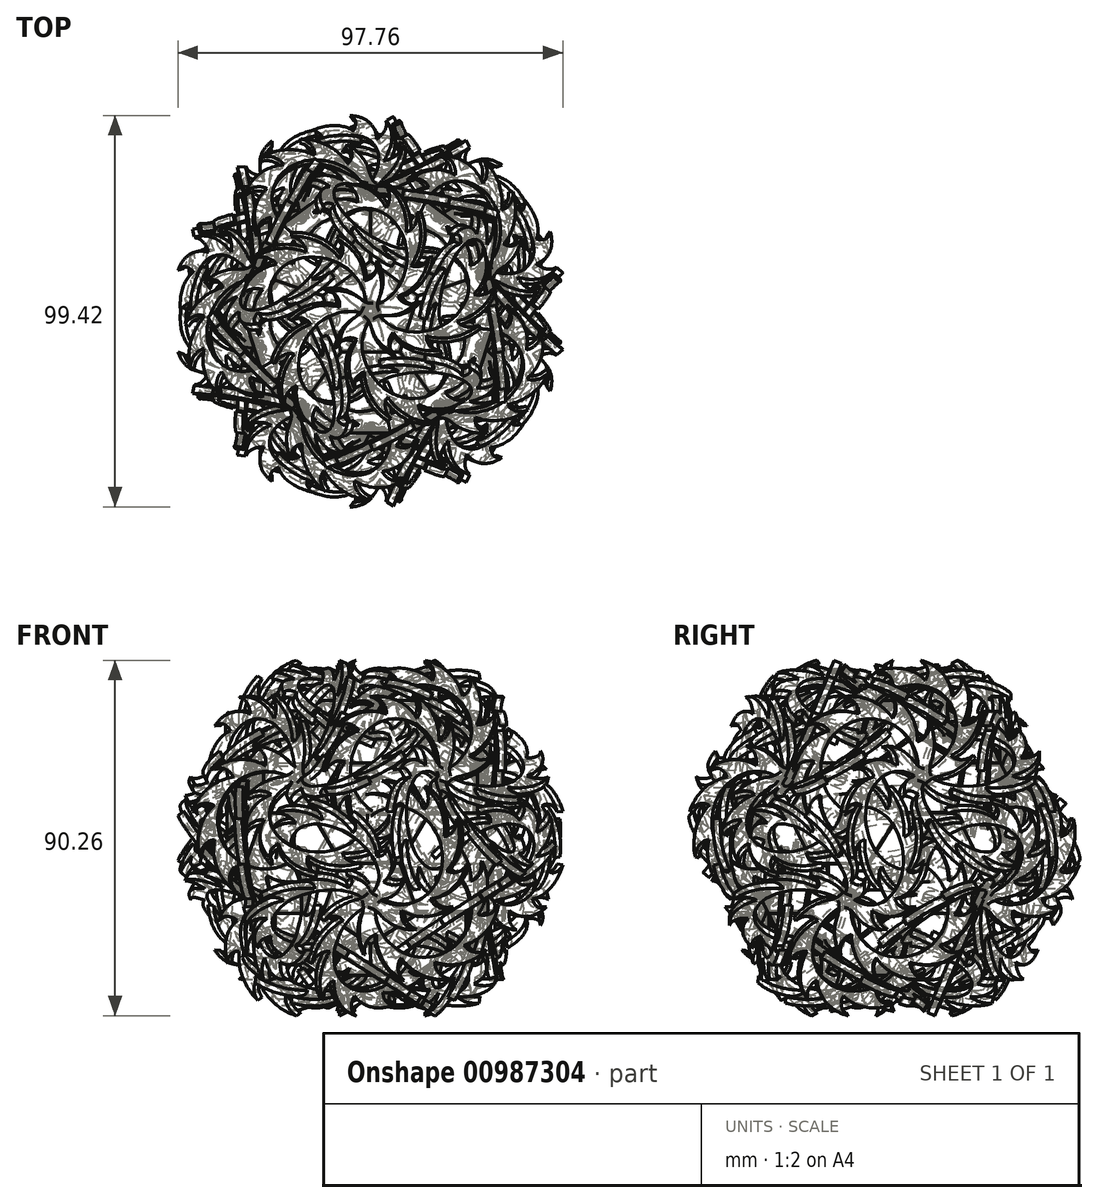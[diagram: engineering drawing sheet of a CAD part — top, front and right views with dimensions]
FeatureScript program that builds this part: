
annotation { "Feature Type Name" : "Feature", "Feature Type Description" : "" }
export const myFeature = defineFeature(function(context is Context, id is Id, definition is map)
    precondition{}
    {
        {
            var Q0;
            Q0=qCreatedBy(makeId("Top.planeOp"),FACE);
            var sketch = newSketch(context, id + "F0", { "sketchPlane" : qUnion([Q0])});
            skCircle(sketch, "E0.cCircle", {"center": v(0, 0) * mm, "radius": 10.32 * mm, "construction": true});
            skLineSegment(sketch, "E0.0", {"start": v(7.5, -10.32) * mm, "end": v(-7.5, -10.32) * mm});
            skLineSegment(sketch, "E0.1", {"start": v(-7.5, -10.32) * mm, "end": v(-12.14, 3.94) * mm});
            skLineSegment(sketch, "E0.2", {"start": v(-12.14, 3.94) * mm, "end": v(0, 12.76) * mm});
            skLineSegment(sketch, "E0.3", {"start": v(0, 12.76) * mm, "end": v(12.14, 3.94) * mm});
            skLineSegment(sketch, "E0.4", {"start": v(12.14, 3.94) * mm, "end": v(7.5, -10.32) * mm});
            skPoint(sketch, "E0.0.midPoint", {"position": v(0, -10.32) * mm});
            skLineSegment(sketch, "E1", {"start": v(0, 12.76) * mm, "end": v(0, -10.32) * mm});
            skSolve(sketch);
        }
        {
            var Q0;
            Q0=qCreatedBy(makeId("Top.planeOp"),FACE);
            var sketch = newSketch(context, id + "F1", { "sketchPlane" : qUnion([Q0])});
            skCircle(sketch, "E2.cCircle", {"center": v(22.17, -7.2) * mm, "radius": 13 * mm, "construction": true});
            skLineSegment(sketch, "E2.0", {"start": v(36.84, -4.09) * mm, "end": v(32.2, -18.35) * mm});
            skLineSegment(sketch, "E2.1", {"start": v(32.2, -18.35) * mm, "end": v(17.54, -21.47) * mm});
            skLineSegment(sketch, "E2.2", {"start": v(17.54, -21.47) * mm, "end": v(7.5, -10.32) * mm});
            skLineSegment(sketch, "E2.3", {"start": v(7.5, -10.32) * mm, "end": v(12.14, 3.94) * mm});
            skLineSegment(sketch, "E2.4", {"start": v(12.14, 3.94) * mm, "end": v(26.8, 7.06) * mm});
            skLineSegment(sketch, "E2.5", {"start": v(26.8, 7.06) * mm, "end": v(36.84, -4.09) * mm});
            skPoint(sketch, "E2.0.midPoint", {"position": v(34.53, -11.22) * mm});
            skSolve(sketch);
        }
        {
            var Q0;
            Q0=makeQuery(id+"F0.imprint","IMPRINT",FACE,{"disambiguationData":[TD([[makeQuery(id+"F0.imprint","IMPRINT",EDGE,{"derivedFrom":sQuery(id+"F0.wireOp",EDGE,"E0.0")}),-1.0]])]});
            extrude(context, id + "F2", {"entities" : qUnion([Q0]), "oppositeDirection" : true, "depth" : 1 * mm, "offsetDistance" : 25 * mm});
        }
        {
            var Q0;
            Q0=makeQuery(id+"F1.imprint","IMPRINT",FACE,{"disambiguationData":[TD([[makeQuery(id+"F1.imprint","IMPRINT",EDGE,{"derivedFrom":sQuery(id+"F1.wireOp",EDGE,"E2.0")}),-1.0]])]});
            extrude(context, id + "F3", {"entities" : qUnion([Q0]), "oppositeDirection" : true, "depth" : 1 * mm, "offsetDistance" : 25 * mm});
        }
        {
            var Q0;
            Q0=makeQuery(id+"F3.opExtrude","SWEPT_BODY",BODY,{"disambiguationData":[OSD([sQuery(id+"F1.wireOp",EDGE,"E2.0"),sQuery(id+"F1.wireOp",EDGE,"E2.1"),sQuery(id+"F1.wireOp",EDGE,"E2.2"),sQuery(id+"F1.wireOp",EDGE,"E2.3"),sQuery(id+"F1.wireOp",EDGE,"E2.4"),sQuery(id+"F1.wireOp",EDGE,"E2.5")])]});
            var Q1;
            Q1=makeQuery(id+"F2.opExtrude","CAP_EDGE",EDGE,{"disambiguationData":[OSD([sQuery(id+"F0.wireOp",EDGE,"E0.4")])],"isStart":true});
            transform(context, id + "F4", {"entities" : qUnion([Q0]), "transformType" : TransformType.ROTATION, "transformAxis" : qUnion([Q1]), "angle" : 37.38 * degree, "oppositeDirection" : true, "makeCopy" : false});
        }
        {
            var Q0;
            Q0=qCreatedBy(makeId("Right.planeOp"),FACE);
            var sketch = newSketch(context, id + "F5", { "sketchPlane" : qUnion([Q0])});
            skLineSegment(sketch, "E3", {"start": v(0, 0) * mm, "end": v(0, 7.73) * mm});
            skSolve(sketch);
        }
        {
            var Q0;
            Q0=makeQuery(id+"F3.opExtrude","SWEPT_BODY",BODY,{"disambiguationData":[OSD([sQuery(id+"F1.wireOp",EDGE,"E2.0"),sQuery(id+"F1.wireOp",EDGE,"E2.1"),sQuery(id+"F1.wireOp",EDGE,"E2.2"),sQuery(id+"F1.wireOp",EDGE,"E2.3"),sQuery(id+"F1.wireOp",EDGE,"E2.4"),sQuery(id+"F1.wireOp",EDGE,"E2.5")])]});
            var Q1;
            Q1=sQuery(id+"F5.wireOp",EDGE,"E3");
            circularPattern(context, id + "F6", {"entities" : qUnion([Q0]), "axis" : qUnion([Q1]), "angle" : 72 * degree, "instanceCount" : round(5)});
        }
        {
            var Q0;
            Q0=makeQuery(id+"F6.opPattern","COPY",FACE,{"derivedFrom":makeQuery(id+"F3.opExtrude","CAP_FACE",FACE,{"disambiguationData":[OSD([sQuery(id+"F1.wireOp",EDGE,"E2.0"),sQuery(id+"F1.wireOp",EDGE,"E2.1"),sQuery(id+"F1.wireOp",EDGE,"E2.2"),sQuery(id+"F1.wireOp",EDGE,"E2.3"),sQuery(id+"F1.wireOp",EDGE,"E2.4"),sQuery(id+"F1.wireOp",EDGE,"E2.5")])],"isStart":true}),"instanceName":"4"});
            var sketch = newSketch(context, id + "F7", { "sketchPlane" : qUnion([Q0])});
            skLineSegment(sketch, "E4", {"start": v(0, -34.18) * mm, "end": v(0, -8.2) * mm});
            skLineSegment(sketch, "E5", {"start": v(-15, -21.2) * mm, "end": v(15, -21.2) * mm});
            skCircle(sketch, "E6", {"center": v(0, -21.2) * mm, "radius": 3.24 * mm});
            skSolve(sketch);
        }
        {
            var Q0;
            Q0=qCreatedBy(makeId("Right.planeOp"),FACE);
            var sketch = newSketch(context, id + "F8", { "sketchPlane" : qUnion([Q0])});
            skArc(sketch, "E7.0", {"start": v(-1.37, 0) * mm, "mid": v(-18.04, 14.75) * mm, "end": v(-20.04, -7.42) * mm});
            skLineSegment(sketch, "E8", {"start": v(-20.04, -7.42) * mm, "end": v(-24.47, -10.8) * mm});
            skLineSegment(sketch, "E9", {"start": v(-1.37, 0) * mm, "end": v(0, 0) * mm});
            skArc(sketch, "E10", {"start": v(1.07, 1.27) * mm, "mid": v(3.46, 7.37) * mm, "end": v(2.5, 13.85) * mm});
            skArc(sketch, "E11", {"start": v(-0.8, 8.97) * mm, "mid": v(1.84, 10.74) * mm, "end": v(2.5, 13.85) * mm});
            skArc(sketch, "E12.1.0", {"start": v(-0.8, 8.97) * mm, "mid": v(-2.13, 15.94) * mm, "end": v(-6.98, 21.1) * mm});
            skArc(sketch, "E12.1.1", {"start": v(-6.75, 15.32) * mm, "mid": v(-5.72, 18.26) * mm, "end": v(-6.98, 21.1) * mm});
            skArc(sketch, "E12.2.0", {"start": v(-6.75, 15.32) * mm, "mid": v(-11.92, 20.18) * mm, "end": v(-18.89, 21.5) * mm});
            skArc(sketch, "E12.2.1", {"start": v(-15.3, 16.96) * mm, "mid": v(-16.2, 19.94) * mm, "end": v(-18.89, 21.5) * mm});
            skArc(sketch, "E12.3.0", {"start": v(-15.3, 16.96) * mm, "mid": v(-22.34, 17.85) * mm, "end": v(-28.75, 14.83) * mm});
            skArc(sketch, "E12.3.1", {"start": v(-23.18, 13.26) * mm, "mid": v(-25.66, 15.15) * mm, "end": v(-28.75, 14.83) * mm});
            skArc(sketch, "E12.4.0", {"start": v(-23.18, 13.26) * mm, "mid": v(-29.4, 9.84) * mm, "end": v(-32.81, 3.63) * mm});
            skArc(sketch, "E12.4.1", {"start": v(-27.38, 5.64) * mm, "mid": v(-30.5, 5.7) * mm, "end": v(-32.81, 3.63) * mm});
            skArc(sketch, "E12.5.0", {"start": v(-27.38, 5.64) * mm, "mid": v(-30.4, -0.78) * mm, "end": v(-29.51, -7.81) * mm});
            skArc(sketch, "E12.5.1", {"start": v(-26.3, -3) * mm, "mid": v(-28.86, -4.77) * mm, "end": v(-29.51, -7.81) * mm});
            skArc(sketch, "E12.6.0", {"start": v(-26.3, -3) * mm, "mid": v(-26.03, -7.06) * mm, "end": v(-24.49, -10.82) * mm});
            skArc(sketch, "E13", {"start": v(-24.49, -10.82) * mm, "mid": v(-20.56, -11.35) * mm, "end": v(-20.04, -7.42) * mm});
            skArc(sketch, "E14", {"start": v(-1.37, 0) * mm, "mid": v(1.27, -2.11) * mm, "end": v(1.07, 1.27) * mm});
            skSolve(sketch);
        }
        {
            var Q0;
            {var subQ2=sQuery(id+"F8.wireOp",EDGE,"E7.0");Q0=makeQuery(id+"F8.imprint","IMPRINT",FACE,{"disambiguationData":[TD([[makeQuery(id+"F8.imprint","IMPRINT",EDGE,{"derivedFrom":subQ2}),-1.0]])]});}
            extrude(context, id + "F9", {"entities" : qUnion([Q0]), "oppositeDirection" : true, "depth" : 2 * mm});
        }
        {
            var Q0;
            Q0=makeQuery(id+"F9.opExtrude","SWEPT_EDGE",EDGE,{"disambiguationData":[OSD([sQuery(id+"F8.wireOp",EDGE,"E10"),sQuery(id+"F8.wireOp",EDGE,"E14")])]});
            fillet(context, id + "F10", {"entities" : qUnion([Q0]), "radius" : 5 * mm, "tangentPropagation" : true, "allowEdgeOverflow" : false});
        }
        {
            var Q0;
            Q0=qCreatedBy(makeId("Right.planeOp"),FACE);
            var sketch = newSketch(context, id + "F11", { "sketchPlane" : qUnion([Q0])});
            skLineSegment(sketch, "E15", {"start": v(0, 0) * mm, "end": v(-20.65, -7.89) * mm});
            skLineSegment(sketch, "E16", {"start": v(0, 0) * mm, "end": v(0, 28.42) * mm});
            skSolve(sketch);
        }
        {
            var Q0;
            Q0=makeQuery(id+"F9.opExtrude","SWEPT_BODY",BODY,{"disambiguationData":[OSD([sQuery(id+"F8.wireOp",EDGE,"003f2e54-bd62-4f0b-a98e-8c36e71e2cf6"),sQuery(id+"F8.wireOp",EDGE,"8c729305-40a1-49fa-b790-4b99a3909bb6"),sQuery(id+"F8.wireOp",EDGE,"862a2a8f-3db7-4421-9c69-6ab2f53c4c24.1.0"),sQuery(id+"F8.wireOp",EDGE,"862a2a8f-3db7-4421-9c69-6ab2f53c4c24.1.1"),sQuery(id+"F8.wireOp",EDGE,"862a2a8f-3db7-4421-9c69-6ab2f53c4c24.2.0"),sQuery(id+"F8.wireOp",EDGE,"862a2a8f-3db7-4421-9c69-6ab2f53c4c24.2.1"),sQuery(id+"F8.wireOp",EDGE,"862a2a8f-3db7-4421-9c69-6ab2f53c4c24.3.0"),sQuery(id+"F8.wireOp",EDGE,"862a2a8f-3db7-4421-9c69-6ab2f53c4c24.3.1"),sQuery(id+"F8.wireOp",EDGE,"862a2a8f-3db7-4421-9c69-6ab2f53c4c24.4.0"),sQuery(id+"F8.wireOp",EDGE,"862a2a8f-3db7-4421-9c69-6ab2f53c4c24.4.1"),sQuery(id+"F8.wireOp",EDGE,"862a2a8f-3db7-4421-9c69-6ab2f53c4c24.5.0"),sQuery(id+"F8.wireOp",EDGE,"E7.0"),sQuery(id+"F8.wireOp",EDGE,"E8"),sQuery(id+"F8.wireOp",EDGE,"E9")])]});
            var Q1;
            Q1=sQuery(id+"F11.wireOp",EDGE,"E15");
            transform(context, id + "F12", {"entities" : qUnion([Q0]), "transformType" : TransformType.ROTATION, "transformAxis" : qUnion([Q1]), "angle" : 65 * degree, "makeCopy" : false});
        }
        {
            var Q0;
            Q0=makeQuery(id+"F9.opExtrude","SWEPT_BODY",BODY,{"disambiguationData":[OSD([sQuery(id+"F8.wireOp",EDGE,"003f2e54-bd62-4f0b-a98e-8c36e71e2cf6"),sQuery(id+"F8.wireOp",EDGE,"8c729305-40a1-49fa-b790-4b99a3909bb6"),sQuery(id+"F8.wireOp",EDGE,"862a2a8f-3db7-4421-9c69-6ab2f53c4c24.1.0"),sQuery(id+"F8.wireOp",EDGE,"862a2a8f-3db7-4421-9c69-6ab2f53c4c24.1.1"),sQuery(id+"F8.wireOp",EDGE,"862a2a8f-3db7-4421-9c69-6ab2f53c4c24.2.0"),sQuery(id+"F8.wireOp",EDGE,"862a2a8f-3db7-4421-9c69-6ab2f53c4c24.2.1"),sQuery(id+"F8.wireOp",EDGE,"862a2a8f-3db7-4421-9c69-6ab2f53c4c24.3.0"),sQuery(id+"F8.wireOp",EDGE,"862a2a8f-3db7-4421-9c69-6ab2f53c4c24.3.1"),sQuery(id+"F8.wireOp",EDGE,"862a2a8f-3db7-4421-9c69-6ab2f53c4c24.4.0"),sQuery(id+"F8.wireOp",EDGE,"862a2a8f-3db7-4421-9c69-6ab2f53c4c24.4.1"),sQuery(id+"F8.wireOp",EDGE,"862a2a8f-3db7-4421-9c69-6ab2f53c4c24.5.0"),sQuery(id+"F8.wireOp",EDGE,"E7.0"),sQuery(id+"F8.wireOp",EDGE,"E8"),sQuery(id+"F8.wireOp",EDGE,"E9")])]});
            var Q1;
            Q1=sQuery(id+"F11.wireOp",EDGE,"E16");
            circularPattern(context, id + "F13", {"entities" : qUnion([Q0]), "axis" : qUnion([Q1]), "angle" : 72 * degree, "instanceCount" : round(5)});
        }
        {
            var Q0;
            Q0=qCreatedBy(makeId("Right.planeOp"),FACE);
            var sketch = newSketch(context, id + "F14", { "sketchPlane" : qUnion([Q0])});
            skLineSegment(sketch, "E17.0", {"start": v(-30.97, -15.77) * mm, "end": v(-10.32, 0) * mm});
            skLineSegment(sketch, "E18", {"start": v(-20.65, -7.89) * mm, "end": v(-30.05, 4.42) * mm});
            skSolve(sketch);
        }
        {
            var Q0;
            Q0=makeQuery(id+"F9.opExtrude","SWEPT_BODY",BODY,{"disambiguationData":[OSD([sQuery(id+"F8.wireOp",EDGE,"003f2e54-bd62-4f0b-a98e-8c36e71e2cf6"),sQuery(id+"F8.wireOp",EDGE,"8c729305-40a1-49fa-b790-4b99a3909bb6"),sQuery(id+"F8.wireOp",EDGE,"862a2a8f-3db7-4421-9c69-6ab2f53c4c24.1.0"),sQuery(id+"F8.wireOp",EDGE,"862a2a8f-3db7-4421-9c69-6ab2f53c4c24.1.1"),sQuery(id+"F8.wireOp",EDGE,"862a2a8f-3db7-4421-9c69-6ab2f53c4c24.2.0"),sQuery(id+"F8.wireOp",EDGE,"862a2a8f-3db7-4421-9c69-6ab2f53c4c24.2.1"),sQuery(id+"F8.wireOp",EDGE,"862a2a8f-3db7-4421-9c69-6ab2f53c4c24.3.0"),sQuery(id+"F8.wireOp",EDGE,"862a2a8f-3db7-4421-9c69-6ab2f53c4c24.3.1"),sQuery(id+"F8.wireOp",EDGE,"862a2a8f-3db7-4421-9c69-6ab2f53c4c24.4.0"),sQuery(id+"F8.wireOp",EDGE,"862a2a8f-3db7-4421-9c69-6ab2f53c4c24.4.1"),sQuery(id+"F8.wireOp",EDGE,"862a2a8f-3db7-4421-9c69-6ab2f53c4c24.5.0"),sQuery(id+"F8.wireOp",EDGE,"E7.0"),sQuery(id+"F8.wireOp",EDGE,"E8"),sQuery(id+"F8.wireOp",EDGE,"E9")])]});
            var Q1;
            Q1=sQuery(id+"F14.wireOp",EDGE,"E18");
            circularPattern(context, id + "F15", {"entities" : qUnion([Q0]), "axis" : qUnion([Q1]), "angle" : 120 * degree, "instanceCount" : round(3)});
        }
        {
            var Q0;
            Q0=makeQuery(id+"F15.opPattern","COPY",BODY,{"derivedFrom":makeQuery(id+"F9.opExtrude","SWEPT_BODY",BODY,{"disambiguationData":[OSD([sQuery(id+"F8.wireOp",EDGE,"E7.0"),sQuery(id+"F8.wireOp",EDGE,"E10"),sQuery(id+"F8.wireOp",EDGE,"E11"),sQuery(id+"F8.wireOp",EDGE,"E12.1.0"),sQuery(id+"F8.wireOp",EDGE,"E12.1.1"),sQuery(id+"F8.wireOp",EDGE,"E12.2.0"),sQuery(id+"F8.wireOp",EDGE,"E12.2.1"),sQuery(id+"F8.wireOp",EDGE,"E12.3.0"),sQuery(id+"F8.wireOp",EDGE,"E12.3.1"),sQuery(id+"F8.wireOp",EDGE,"E12.4.0"),sQuery(id+"F8.wireOp",EDGE,"E12.4.1"),sQuery(id+"F8.wireOp",EDGE,"E12.5.0"),sQuery(id+"F8.wireOp",EDGE,"E12.5.1"),sQuery(id+"F8.wireOp",EDGE,"E12.6.0"),sQuery(id+"F8.wireOp",EDGE,"E13"),sQuery(id+"F8.wireOp",EDGE,"E14")])]}),"instanceName":"2"});
            var Q1;
            Q1=makeQuery(id+"F15.opPattern","COPY",BODY,{"derivedFrom":makeQuery(id+"F9.opExtrude","SWEPT_BODY",BODY,{"disambiguationData":[OSD([sQuery(id+"F8.wireOp",EDGE,"E7.0"),sQuery(id+"F8.wireOp",EDGE,"E10"),sQuery(id+"F8.wireOp",EDGE,"E11"),sQuery(id+"F8.wireOp",EDGE,"E12.1.0"),sQuery(id+"F8.wireOp",EDGE,"E12.1.1"),sQuery(id+"F8.wireOp",EDGE,"E12.2.0"),sQuery(id+"F8.wireOp",EDGE,"E12.2.1"),sQuery(id+"F8.wireOp",EDGE,"E12.3.0"),sQuery(id+"F8.wireOp",EDGE,"E12.3.1"),sQuery(id+"F8.wireOp",EDGE,"E12.4.0"),sQuery(id+"F8.wireOp",EDGE,"E12.4.1"),sQuery(id+"F8.wireOp",EDGE,"E12.5.0"),sQuery(id+"F8.wireOp",EDGE,"E12.5.1"),sQuery(id+"F8.wireOp",EDGE,"E12.6.0"),sQuery(id+"F8.wireOp",EDGE,"E13"),sQuery(id+"F8.wireOp",EDGE,"E14")])]}),"instanceName":"1"});
            var Q2;
            Q2=sQuery(id+"F11.wireOp",EDGE,"E16");
            circularPattern(context, id + "F16", {"entities" : qUnion([Q0, Q1]), "axis" : qUnion([Q2]), "angle" : 72 * degree, "instanceCount" : round(5)});
        }
        {
            var Q0;
            Q0=makeQuery(id+"F3.opExtrude","SWEPT_BODY",BODY,{"disambiguationData":[OSD([sQuery(id+"F1.wireOp",EDGE,"E2.0"),sQuery(id+"F1.wireOp",EDGE,"E2.1"),sQuery(id+"F1.wireOp",EDGE,"E2.2"),sQuery(id+"F1.wireOp",EDGE,"E2.3"),sQuery(id+"F1.wireOp",EDGE,"E2.4"),sQuery(id+"F1.wireOp",EDGE,"E2.5")])]});
            var Q1;
            Q1=makeQuery(id+"F16.opPattern","COPY",BODY,{"derivedFrom":makeQuery(id+"F15.opPattern","COPY",BODY,{"derivedFrom":makeQuery(id+"F9.opExtrude","SWEPT_BODY",BODY,{"disambiguationData":[OSD([sQuery(id+"F8.wireOp",EDGE,"E7.0"),sQuery(id+"F8.wireOp",EDGE,"E10"),sQuery(id+"F8.wireOp",EDGE,"E11"),sQuery(id+"F8.wireOp",EDGE,"E12.1.0"),sQuery(id+"F8.wireOp",EDGE,"E12.1.1"),sQuery(id+"F8.wireOp",EDGE,"E12.2.0"),sQuery(id+"F8.wireOp",EDGE,"E12.2.1"),sQuery(id+"F8.wireOp",EDGE,"E12.3.0"),sQuery(id+"F8.wireOp",EDGE,"E12.3.1"),sQuery(id+"F8.wireOp",EDGE,"E12.4.0"),sQuery(id+"F8.wireOp",EDGE,"E12.4.1"),sQuery(id+"F8.wireOp",EDGE,"E12.5.0"),sQuery(id+"F8.wireOp",EDGE,"E12.5.1"),sQuery(id+"F8.wireOp",EDGE,"E12.6.0"),sQuery(id+"F8.wireOp",EDGE,"E13"),sQuery(id+"F8.wireOp",EDGE,"E14")])]}),"instanceName":"1"}),"instanceName":"1"});
            var Q2;
            Q2=makeQuery(id+"F13.opPattern","COPY",BODY,{"derivedFrom":makeQuery(id+"F9.opExtrude","SWEPT_BODY",BODY,{"disambiguationData":[OSD([sQuery(id+"F8.wireOp",EDGE,"E7.0"),sQuery(id+"F8.wireOp",EDGE,"E10"),sQuery(id+"F8.wireOp",EDGE,"E11"),sQuery(id+"F8.wireOp",EDGE,"E12.1.0"),sQuery(id+"F8.wireOp",EDGE,"E12.1.1"),sQuery(id+"F8.wireOp",EDGE,"E12.2.0"),sQuery(id+"F8.wireOp",EDGE,"E12.2.1"),sQuery(id+"F8.wireOp",EDGE,"E12.3.0"),sQuery(id+"F8.wireOp",EDGE,"E12.3.1"),sQuery(id+"F8.wireOp",EDGE,"E12.4.0"),sQuery(id+"F8.wireOp",EDGE,"E12.4.1"),sQuery(id+"F8.wireOp",EDGE,"E12.5.0"),sQuery(id+"F8.wireOp",EDGE,"E12.5.1"),sQuery(id+"F8.wireOp",EDGE,"E12.6.0"),sQuery(id+"F8.wireOp",EDGE,"E13"),sQuery(id+"F8.wireOp",EDGE,"E14")])]}),"instanceName":"1"});
            var Q3;
            Q3=makeQuery(id+"F16.opPattern","COPY",BODY,{"derivedFrom":makeQuery(id+"F15.opPattern","COPY",BODY,{"derivedFrom":makeQuery(id+"F9.opExtrude","SWEPT_BODY",BODY,{"disambiguationData":[OSD([sQuery(id+"F8.wireOp",EDGE,"E7.0"),sQuery(id+"F8.wireOp",EDGE,"E10"),sQuery(id+"F8.wireOp",EDGE,"E11"),sQuery(id+"F8.wireOp",EDGE,"E12.1.0"),sQuery(id+"F8.wireOp",EDGE,"E12.1.1"),sQuery(id+"F8.wireOp",EDGE,"E12.2.0"),sQuery(id+"F8.wireOp",EDGE,"E12.2.1"),sQuery(id+"F8.wireOp",EDGE,"E12.3.0"),sQuery(id+"F8.wireOp",EDGE,"E12.3.1"),sQuery(id+"F8.wireOp",EDGE,"E12.4.0"),sQuery(id+"F8.wireOp",EDGE,"E12.4.1"),sQuery(id+"F8.wireOp",EDGE,"E12.5.0"),sQuery(id+"F8.wireOp",EDGE,"E12.5.1"),sQuery(id+"F8.wireOp",EDGE,"E12.6.0"),sQuery(id+"F8.wireOp",EDGE,"E13"),sQuery(id+"F8.wireOp",EDGE,"E14")])]}),"instanceName":"2"}),"instanceName":"1"});
            var Q4;
            Q4=sQuery(id+"F14.wireOp",EDGE,"E18");
            circularPattern(context, id + "F17", {"entities" : qUnion([Q0, Q1, Q2, Q3]), "axis" : qUnion([Q4]), "angle" : 120 * degree, "instanceCount" : 2, "oppositeDirection" : true});
        }
        {
            var Q0;
            Q0=makeQuery(id+"F2.opExtrude","SWEPT_BODY",BODY,{"disambiguationData":[OSD([sQuery(id+"F0.wireOp",EDGE,"E0.0"),sQuery(id+"F0.wireOp",EDGE,"E0.1"),sQuery(id+"F0.wireOp",EDGE,"E0.2"),sQuery(id+"F0.wireOp",EDGE,"E0.3"),sQuery(id+"F0.wireOp",EDGE,"E0.4")])]});
            var Q1;
            Q1=makeQuery(id+"F13.opPattern","COPY",BODY,{"derivedFrom":makeQuery(id+"F9.opExtrude","SWEPT_BODY",BODY,{"disambiguationData":[OSD([sQuery(id+"F8.wireOp",EDGE,"E7.0"),sQuery(id+"F8.wireOp",EDGE,"E10"),sQuery(id+"F8.wireOp",EDGE,"E11"),sQuery(id+"F8.wireOp",EDGE,"E12.1.0"),sQuery(id+"F8.wireOp",EDGE,"E12.1.1"),sQuery(id+"F8.wireOp",EDGE,"E12.2.0"),sQuery(id+"F8.wireOp",EDGE,"E12.2.1"),sQuery(id+"F8.wireOp",EDGE,"E12.3.0"),sQuery(id+"F8.wireOp",EDGE,"E12.3.1"),sQuery(id+"F8.wireOp",EDGE,"E12.4.0"),sQuery(id+"F8.wireOp",EDGE,"E12.4.1"),sQuery(id+"F8.wireOp",EDGE,"E12.5.0"),sQuery(id+"F8.wireOp",EDGE,"E12.5.1"),sQuery(id+"F8.wireOp",EDGE,"E12.6.0"),sQuery(id+"F8.wireOp",EDGE,"E13"),sQuery(id+"F8.wireOp",EDGE,"E14")])]}),"instanceName":"2"});
            var Q2;
            Q2=makeQuery(id+"F13.opPattern","COPY",BODY,{"derivedFrom":makeQuery(id+"F9.opExtrude","SWEPT_BODY",BODY,{"disambiguationData":[OSD([sQuery(id+"F8.wireOp",EDGE,"E7.0"),sQuery(id+"F8.wireOp",EDGE,"E10"),sQuery(id+"F8.wireOp",EDGE,"E11"),sQuery(id+"F8.wireOp",EDGE,"E12.1.0"),sQuery(id+"F8.wireOp",EDGE,"E12.1.1"),sQuery(id+"F8.wireOp",EDGE,"E12.2.0"),sQuery(id+"F8.wireOp",EDGE,"E12.2.1"),sQuery(id+"F8.wireOp",EDGE,"E12.3.0"),sQuery(id+"F8.wireOp",EDGE,"E12.3.1"),sQuery(id+"F8.wireOp",EDGE,"E12.4.0"),sQuery(id+"F8.wireOp",EDGE,"E12.4.1"),sQuery(id+"F8.wireOp",EDGE,"E12.5.0"),sQuery(id+"F8.wireOp",EDGE,"E12.5.1"),sQuery(id+"F8.wireOp",EDGE,"E12.6.0"),sQuery(id+"F8.wireOp",EDGE,"E13"),sQuery(id+"F8.wireOp",EDGE,"E14")])]}),"instanceName":"3"});
            var Q3;
            Q3=sQuery(id+"F14.wireOp",EDGE,"E18");
            circularPattern(context, id + "F18", {"entities" : qUnion([Q0, Q1, Q2]), "axis" : qUnion([Q3]), "angle" : 120 * degree, "instanceCount" : round(3)});
        }
        {
            var Q0;
            Q0=makeQuery(id+"F18.opPattern","COPY",FACE,{"derivedFrom":makeQuery(id+"F2.opExtrude","CAP_FACE",FACE,{"disambiguationData":[OSD([sQuery(id+"F0.wireOp",EDGE,"E0.0"),sQuery(id+"F0.wireOp",EDGE,"E0.1"),sQuery(id+"F0.wireOp",EDGE,"E0.2"),sQuery(id+"F0.wireOp",EDGE,"E0.3"),sQuery(id+"F0.wireOp",EDGE,"E0.4")])],"isStart":true}),"instanceName":"1"});
            var sketch = newSketch(context, id + "F19", { "sketchPlane" : qUnion([Q0])});
            skLineSegment(sketch, "E19", {"start": v(-1.3, -23.63) * mm, "end": v(-19.97, -37.2) * mm});
            skLineSegment(sketch, "E20", {"start": v(-19.97, -22.2) * mm, "end": v(-1.3, -35.77) * mm});
            skSolve(sketch);
        }
        {
            var Q0;
            Q0=sQuery(id+"F19.wireOp",VERTEX,"E19.end");
            var Q1;
            Q1=sQuery(id+"F19.wireOp",VERTEX,"E19.start");
            var Q2;
            Q2=sQuery(id+"F14.wireOp",VERTEX,"E18.end");
            cPlane(context, id + "F20", {"entities" : qUnion([Q0, Q1, Q2]), "cplaneType" : CPlaneType.THREE_POINT, "offset" : 150 * mm, "width" : 150 * mm, "height" : 150 * mm});
        }
        {
            var Q0;
            Q0=qCreatedBy(id+"F20.planeOp",FACE);
            var sketch = newSketch(context, id + "F21", { "sketchPlane" : qUnion([Q0])});
            skLineSegment(sketch, "E21.0", {"start": v(23.59, 6.27) * mm, "end": v(41.93, -7.75) * mm});
            skLineSegment(sketch, "E21.1", {"start": v(34.92, -2.4) * mm, "end": v(29.26, 1.94) * mm});
            skLineSegment(sketch, "E22", {"start": v(31.8, 0) * mm, "end": v(33.22, 1.87) * mm});
            skLineSegment(sketch, "E23", {"start": v(33.22, 1.87) * mm, "end": v(37.58, 7.58) * mm});
            skSolve(sketch);
        }
        {
            var Q0;
            Q0=makeQuery(id+"F17.opPattern","COPY",BODY,{"derivedFrom":makeQuery(id+"F3.opExtrude","SWEPT_BODY",BODY,{"disambiguationData":[OSD([sQuery(id+"F1.wireOp",EDGE,"E2.0"),sQuery(id+"F1.wireOp",EDGE,"E2.1"),sQuery(id+"F1.wireOp",EDGE,"E2.2"),sQuery(id+"F1.wireOp",EDGE,"E2.3"),sQuery(id+"F1.wireOp",EDGE,"E2.4"),sQuery(id+"F1.wireOp",EDGE,"E2.5")])]}),"instanceName":"1"});
            var Q1;
            Q1=makeQuery(id+"F17.opPattern","COPY",BODY,{"derivedFrom":makeQuery(id+"F13.opPattern","COPY",BODY,{"derivedFrom":makeQuery(id+"F9.opExtrude","SWEPT_BODY",BODY,{"disambiguationData":[OSD([sQuery(id+"F8.wireOp",EDGE,"E7.0"),sQuery(id+"F8.wireOp",EDGE,"E10"),sQuery(id+"F8.wireOp",EDGE,"E11"),sQuery(id+"F8.wireOp",EDGE,"E12.1.0"),sQuery(id+"F8.wireOp",EDGE,"E12.1.1"),sQuery(id+"F8.wireOp",EDGE,"E12.2.0"),sQuery(id+"F8.wireOp",EDGE,"E12.2.1"),sQuery(id+"F8.wireOp",EDGE,"E12.3.0"),sQuery(id+"F8.wireOp",EDGE,"E12.3.1"),sQuery(id+"F8.wireOp",EDGE,"E12.4.0"),sQuery(id+"F8.wireOp",EDGE,"E12.4.1"),sQuery(id+"F8.wireOp",EDGE,"E12.5.0"),sQuery(id+"F8.wireOp",EDGE,"E12.5.1"),sQuery(id+"F8.wireOp",EDGE,"E12.6.0"),sQuery(id+"F8.wireOp",EDGE,"E13"),sQuery(id+"F8.wireOp",EDGE,"E14")])]}),"instanceName":"1"}),"instanceName":"1"});
            var Q2;
            Q2=makeQuery(id+"F17.opPattern","COPY",BODY,{"derivedFrom":makeQuery(id+"F16.opPattern","COPY",BODY,{"derivedFrom":makeQuery(id+"F15.opPattern","COPY",BODY,{"derivedFrom":makeQuery(id+"F9.opExtrude","SWEPT_BODY",BODY,{"disambiguationData":[OSD([sQuery(id+"F8.wireOp",EDGE,"E7.0"),sQuery(id+"F8.wireOp",EDGE,"E10"),sQuery(id+"F8.wireOp",EDGE,"E11"),sQuery(id+"F8.wireOp",EDGE,"E12.1.0"),sQuery(id+"F8.wireOp",EDGE,"E12.1.1"),sQuery(id+"F8.wireOp",EDGE,"E12.2.0"),sQuery(id+"F8.wireOp",EDGE,"E12.2.1"),sQuery(id+"F8.wireOp",EDGE,"E12.3.0"),sQuery(id+"F8.wireOp",EDGE,"E12.3.1"),sQuery(id+"F8.wireOp",EDGE,"E12.4.0"),sQuery(id+"F8.wireOp",EDGE,"E12.4.1"),sQuery(id+"F8.wireOp",EDGE,"E12.5.0"),sQuery(id+"F8.wireOp",EDGE,"E12.5.1"),sQuery(id+"F8.wireOp",EDGE,"E12.6.0"),sQuery(id+"F8.wireOp",EDGE,"E13"),sQuery(id+"F8.wireOp",EDGE,"E14")])]}),"instanceName":"2"}),"instanceName":"1"}),"instanceName":"1"});
            var Q3;
            Q3=makeQuery(id+"F17.opPattern","COPY",BODY,{"derivedFrom":makeQuery(id+"F16.opPattern","COPY",BODY,{"derivedFrom":makeQuery(id+"F15.opPattern","COPY",BODY,{"derivedFrom":makeQuery(id+"F9.opExtrude","SWEPT_BODY",BODY,{"disambiguationData":[OSD([sQuery(id+"F8.wireOp",EDGE,"E7.0"),sQuery(id+"F8.wireOp",EDGE,"E10"),sQuery(id+"F8.wireOp",EDGE,"E11"),sQuery(id+"F8.wireOp",EDGE,"E12.1.0"),sQuery(id+"F8.wireOp",EDGE,"E12.1.1"),sQuery(id+"F8.wireOp",EDGE,"E12.2.0"),sQuery(id+"F8.wireOp",EDGE,"E12.2.1"),sQuery(id+"F8.wireOp",EDGE,"E12.3.0"),sQuery(id+"F8.wireOp",EDGE,"E12.3.1"),sQuery(id+"F8.wireOp",EDGE,"E12.4.0"),sQuery(id+"F8.wireOp",EDGE,"E12.4.1"),sQuery(id+"F8.wireOp",EDGE,"E12.5.0"),sQuery(id+"F8.wireOp",EDGE,"E12.5.1"),sQuery(id+"F8.wireOp",EDGE,"E12.6.0"),sQuery(id+"F8.wireOp",EDGE,"E13"),sQuery(id+"F8.wireOp",EDGE,"E14")])]}),"instanceName":"1"}),"instanceName":"1"}),"instanceName":"1"});
            var Q4;
            Q4=sQuery(id+"F21.wireOp",EDGE,"E22");
            circularPattern(context, id + "F22", {"entities" : qUnion([Q0, Q1, Q2, Q3]), "axis" : qUnion([Q4]), "angle" : 72 * degree, "instanceCount" : round(3), "oppositeDirection" : true});
        }
        {
            var Q0;
            Q0=makeQuery(id+"F18.opPattern","COPY",FACE,{"derivedFrom":makeQuery(id+"F2.opExtrude","CAP_FACE",FACE,{"disambiguationData":[OSD([sQuery(id+"F0.wireOp",EDGE,"E0.0"),sQuery(id+"F0.wireOp",EDGE,"E0.1"),sQuery(id+"F0.wireOp",EDGE,"E0.2"),sQuery(id+"F0.wireOp",EDGE,"E0.3"),sQuery(id+"F0.wireOp",EDGE,"E0.4")])],"isStart":true}),"instanceName":"2"});
            var sketch = newSketch(context, id + "F23", { "sketchPlane" : qUnion([Q0])});
            skLineSegment(sketch, "E24", {"start": v(1.3, -23.63) * mm, "end": v(19.97, -37.2) * mm});
            skLineSegment(sketch, "E25", {"start": v(5.7, -41.83) * mm, "end": v(12.84, -19.88) * mm});
            skSolve(sketch);
        }
        {
            var Q0;
            Q0=sQuery(id+"F23.wireOp",VERTEX,"E24.end");
            var Q1;
            Q1=sQuery(id+"F23.wireOp",VERTEX,"E24.start");
            var Q2;
            Q2=sQuery(id+"F14.wireOp",VERTEX,"E18.end");
            cPlane(context, id + "F24", {"entities" : qUnion([Q0, Q1, Q2]), "cplaneType" : CPlaneType.THREE_POINT, "offset" : 150 * mm, "width" : 150 * mm, "height" : 150 * mm});
        }
        {
            var Q0;
            Q0=qCreatedBy(id+"F24.planeOp",FACE);
            var sketch = newSketch(context, id + "F25", { "sketchPlane" : qUnion([Q0])});
            skLineSegment(sketch, "E26.0", {"start": v(23.59, 6.27) * mm, "end": v(41.93, -7.75) * mm});
            skLineSegment(sketch, "E26.1", {"start": v(34.92, -2.4) * mm, "end": v(29.26, 1.94) * mm});
            skLineSegment(sketch, "E27", {"start": v(31.8, 0) * mm, "end": v(36.23, 5.8) * mm});
            skSolve(sketch);
        }
        {
            var Q0;
            Q0=makeQuery(id+"F3.opExtrude","SWEPT_BODY",BODY,{"disambiguationData":[OSD([sQuery(id+"F1.wireOp",EDGE,"E2.0"),sQuery(id+"F1.wireOp",EDGE,"E2.1"),sQuery(id+"F1.wireOp",EDGE,"E2.2"),sQuery(id+"F1.wireOp",EDGE,"E2.3"),sQuery(id+"F1.wireOp",EDGE,"E2.4"),sQuery(id+"F1.wireOp",EDGE,"E2.5")])]});
            var Q1;
            Q1=makeQuery(id+"F16.opPattern","COPY",BODY,{"derivedFrom":makeQuery(id+"F15.opPattern","COPY",BODY,{"derivedFrom":makeQuery(id+"F9.opExtrude","SWEPT_BODY",BODY,{"disambiguationData":[OSD([sQuery(id+"F8.wireOp",EDGE,"E7.0"),sQuery(id+"F8.wireOp",EDGE,"E10"),sQuery(id+"F8.wireOp",EDGE,"E11"),sQuery(id+"F8.wireOp",EDGE,"E12.1.0"),sQuery(id+"F8.wireOp",EDGE,"E12.1.1"),sQuery(id+"F8.wireOp",EDGE,"E12.2.0"),sQuery(id+"F8.wireOp",EDGE,"E12.2.1"),sQuery(id+"F8.wireOp",EDGE,"E12.3.0"),sQuery(id+"F8.wireOp",EDGE,"E12.3.1"),sQuery(id+"F8.wireOp",EDGE,"E12.4.0"),sQuery(id+"F8.wireOp",EDGE,"E12.4.1"),sQuery(id+"F8.wireOp",EDGE,"E12.5.0"),sQuery(id+"F8.wireOp",EDGE,"E12.5.1"),sQuery(id+"F8.wireOp",EDGE,"E12.6.0"),sQuery(id+"F8.wireOp",EDGE,"E13"),sQuery(id+"F8.wireOp",EDGE,"E14")])]}),"instanceName":"2"}),"instanceName":"1"});
            var Q2;
            Q2=makeQuery(id+"F13.opPattern","COPY",BODY,{"derivedFrom":makeQuery(id+"F9.opExtrude","SWEPT_BODY",BODY,{"disambiguationData":[OSD([sQuery(id+"F8.wireOp",EDGE,"E7.0"),sQuery(id+"F8.wireOp",EDGE,"E10"),sQuery(id+"F8.wireOp",EDGE,"E11"),sQuery(id+"F8.wireOp",EDGE,"E12.1.0"),sQuery(id+"F8.wireOp",EDGE,"E12.1.1"),sQuery(id+"F8.wireOp",EDGE,"E12.2.0"),sQuery(id+"F8.wireOp",EDGE,"E12.2.1"),sQuery(id+"F8.wireOp",EDGE,"E12.3.0"),sQuery(id+"F8.wireOp",EDGE,"E12.3.1"),sQuery(id+"F8.wireOp",EDGE,"E12.4.0"),sQuery(id+"F8.wireOp",EDGE,"E12.4.1"),sQuery(id+"F8.wireOp",EDGE,"E12.5.0"),sQuery(id+"F8.wireOp",EDGE,"E12.5.1"),sQuery(id+"F8.wireOp",EDGE,"E12.6.0"),sQuery(id+"F8.wireOp",EDGE,"E13"),sQuery(id+"F8.wireOp",EDGE,"E14")])]}),"instanceName":"1"});
            var Q3;
            Q3=makeQuery(id+"F16.opPattern","COPY",BODY,{"derivedFrom":makeQuery(id+"F15.opPattern","COPY",BODY,{"derivedFrom":makeQuery(id+"F9.opExtrude","SWEPT_BODY",BODY,{"disambiguationData":[OSD([sQuery(id+"F8.wireOp",EDGE,"E7.0"),sQuery(id+"F8.wireOp",EDGE,"E10"),sQuery(id+"F8.wireOp",EDGE,"E11"),sQuery(id+"F8.wireOp",EDGE,"E12.1.0"),sQuery(id+"F8.wireOp",EDGE,"E12.1.1"),sQuery(id+"F8.wireOp",EDGE,"E12.2.0"),sQuery(id+"F8.wireOp",EDGE,"E12.2.1"),sQuery(id+"F8.wireOp",EDGE,"E12.3.0"),sQuery(id+"F8.wireOp",EDGE,"E12.3.1"),sQuery(id+"F8.wireOp",EDGE,"E12.4.0"),sQuery(id+"F8.wireOp",EDGE,"E12.4.1"),sQuery(id+"F8.wireOp",EDGE,"E12.5.0"),sQuery(id+"F8.wireOp",EDGE,"E12.5.1"),sQuery(id+"F8.wireOp",EDGE,"E12.6.0"),sQuery(id+"F8.wireOp",EDGE,"E13"),sQuery(id+"F8.wireOp",EDGE,"E14")])]}),"instanceName":"1"}),"instanceName":"1"});
            var Q4;
            Q4=sQuery(id+"F25.wireOp",EDGE,"E27");
            circularPattern(context, id + "F26", {"entities" : qUnion([Q0, Q1, Q2, Q3]), "axis" : qUnion([Q4]), "angle" : 72 * degree, "instanceCount" : round(3), "oppositeDirection" : true});
        }
        {
            var Q0;
            Q0=makeQuery(id+"F17.opPattern","COPY",FACE,{"derivedFrom":makeQuery(id+"F3.opExtrude","CAP_FACE",FACE,{"disambiguationData":[OSD([sQuery(id+"F1.wireOp",EDGE,"E2.0"),sQuery(id+"F1.wireOp",EDGE,"E2.1"),sQuery(id+"F1.wireOp",EDGE,"E2.2"),sQuery(id+"F1.wireOp",EDGE,"E2.3"),sQuery(id+"F1.wireOp",EDGE,"E2.4"),sQuery(id+"F1.wireOp",EDGE,"E2.5")])],"isStart":true}),"instanceName":"1"});
            var sketch = newSketch(context, id + "F27", { "sketchPlane" : qUnion([Q0])});
            skLineSegment(sketch, "E28", {"start": v(0, -47.28) * mm, "end": v(0, -21.3) * mm});
            skSolve(sketch);
        }
        {
            var Q0;
            Q0=qCreatedBy(makeId("Right.planeOp"),FACE);
            var sketch = newSketch(context, id + "F28", { "sketchPlane" : qUnion([Q0])});
            skLineSegment(sketch, "E29.0", {"start": v(-35.84, -41.3) * mm, "end": v(-30.97, -15.77) * mm});
            skLineSegment(sketch, "E30", {"start": v(-33.4, -28.53) * mm, "end": v(-47.6, -25.82) * mm});
            skSolve(sketch);
        }
        {
            var Q0;
            Q0=makeQuery(id+"F18.opPattern","COPY",BODY,{"derivedFrom":makeQuery(id+"F2.opExtrude","SWEPT_BODY",BODY,{"disambiguationData":[OSD([sQuery(id+"F0.wireOp",EDGE,"E0.0"),sQuery(id+"F0.wireOp",EDGE,"E0.1"),sQuery(id+"F0.wireOp",EDGE,"E0.2"),sQuery(id+"F0.wireOp",EDGE,"E0.3"),sQuery(id+"F0.wireOp",EDGE,"E0.4")])]}),"instanceName":"2"});
            var Q1;
            Q1=sQuery(id+"F28.wireOp",EDGE,"E30");
            circularPattern(context, id + "F29", {"entities" : qUnion([Q0]), "axis" : qUnion([Q1]), "angle" : 120 * degree, "instanceCount" : 2, "oppositeDirection" : true});
        }
        {
            var Q0;
            Q0=makeQuery(id+"F29.opPattern","COPY",FACE,{"derivedFrom":makeQuery(id+"F18.opPattern","COPY",FACE,{"derivedFrom":makeQuery(id+"F2.opExtrude","CAP_FACE",FACE,{"disambiguationData":[OSD([sQuery(id+"F0.wireOp",EDGE,"E0.0"),sQuery(id+"F0.wireOp",EDGE,"E0.1"),sQuery(id+"F0.wireOp",EDGE,"E0.2"),sQuery(id+"F0.wireOp",EDGE,"E0.3"),sQuery(id+"F0.wireOp",EDGE,"E0.4")])],"isStart":true}),"instanceName":"2"}),"instanceName":"1"});
            var sketch = newSketch(context, id + "F30", { "sketchPlane" : qUnion([Q0])});
            skLineSegment(sketch, "E31", {"start": v(0, -43.99) * mm, "end": v(0, -31.23) * mm});
            skLineSegment(sketch, "E32", {"start": v(-12.14, -35.17) * mm, "end": v(9.82, -28.04) * mm});
            skPoint(sketch, "E33.orphan", {"position": v(0, -20.9) * mm});
            skSolve(sketch);
        }
        {
            var Q0;
            Q0=qCreatedBy(makeId("Right.planeOp"),FACE);
            var sketch = newSketch(context, id + "F31", { "sketchPlane" : qUnion([Q0])});
            skLineSegment(sketch, "E34.0", {"start": v(-25.52, -61.94) * mm, "end": v(-31.23, -50.52) * mm});
            skLineSegment(sketch, "E35", {"start": v(-31.23, -50.52) * mm, "end": v(-51.07, -60.45) * mm});
            skSolve(sketch);
        }
        {
            var Q0;
            Q0=makeQuery(id+"F26.opPattern","COPY",BODY,{"derivedFrom":makeQuery(id+"F3.opExtrude","SWEPT_BODY",BODY,{"disambiguationData":[OSD([sQuery(id+"F1.wireOp",EDGE,"E2.0"),sQuery(id+"F1.wireOp",EDGE,"E2.1"),sQuery(id+"F1.wireOp",EDGE,"E2.2"),sQuery(id+"F1.wireOp",EDGE,"E2.3"),sQuery(id+"F1.wireOp",EDGE,"E2.4"),sQuery(id+"F1.wireOp",EDGE,"E2.5")])]}),"instanceName":"2"});
            var Q1;
            Q1=makeQuery(id+"F26.opPattern","COPY",BODY,{"derivedFrom":makeQuery(id+"F16.opPattern","COPY",BODY,{"derivedFrom":makeQuery(id+"F15.opPattern","COPY",BODY,{"derivedFrom":makeQuery(id+"F9.opExtrude","SWEPT_BODY",BODY,{"disambiguationData":[OSD([sQuery(id+"F8.wireOp",EDGE,"E7.0"),sQuery(id+"F8.wireOp",EDGE,"E10"),sQuery(id+"F8.wireOp",EDGE,"E11"),sQuery(id+"F8.wireOp",EDGE,"E12.1.0"),sQuery(id+"F8.wireOp",EDGE,"E12.1.1"),sQuery(id+"F8.wireOp",EDGE,"E12.2.0"),sQuery(id+"F8.wireOp",EDGE,"E12.2.1"),sQuery(id+"F8.wireOp",EDGE,"E12.3.0"),sQuery(id+"F8.wireOp",EDGE,"E12.3.1"),sQuery(id+"F8.wireOp",EDGE,"E12.4.0"),sQuery(id+"F8.wireOp",EDGE,"E12.4.1"),sQuery(id+"F8.wireOp",EDGE,"E12.5.0"),sQuery(id+"F8.wireOp",EDGE,"E12.5.1"),sQuery(id+"F8.wireOp",EDGE,"E12.6.0"),sQuery(id+"F8.wireOp",EDGE,"E13"),sQuery(id+"F8.wireOp",EDGE,"E14")])]}),"instanceName":"2"}),"instanceName":"1"}),"instanceName":"2"});
            var Q2;
            Q2=makeQuery(id+"F26.opPattern","COPY",BODY,{"derivedFrom":makeQuery(id+"F13.opPattern","COPY",BODY,{"derivedFrom":makeQuery(id+"F9.opExtrude","SWEPT_BODY",BODY,{"disambiguationData":[OSD([sQuery(id+"F8.wireOp",EDGE,"E7.0"),sQuery(id+"F8.wireOp",EDGE,"E10"),sQuery(id+"F8.wireOp",EDGE,"E11"),sQuery(id+"F8.wireOp",EDGE,"E12.1.0"),sQuery(id+"F8.wireOp",EDGE,"E12.1.1"),sQuery(id+"F8.wireOp",EDGE,"E12.2.0"),sQuery(id+"F8.wireOp",EDGE,"E12.2.1"),sQuery(id+"F8.wireOp",EDGE,"E12.3.0"),sQuery(id+"F8.wireOp",EDGE,"E12.3.1"),sQuery(id+"F8.wireOp",EDGE,"E12.4.0"),sQuery(id+"F8.wireOp",EDGE,"E12.4.1"),sQuery(id+"F8.wireOp",EDGE,"E12.5.0"),sQuery(id+"F8.wireOp",EDGE,"E12.5.1"),sQuery(id+"F8.wireOp",EDGE,"E12.6.0"),sQuery(id+"F8.wireOp",EDGE,"E13"),sQuery(id+"F8.wireOp",EDGE,"E14")])]}),"instanceName":"1"}),"instanceName":"2"});
            var Q3;
            Q3=makeQuery(id+"F18.opPattern","COPY",BODY,{"derivedFrom":makeQuery(id+"F13.opPattern","COPY",BODY,{"derivedFrom":makeQuery(id+"F9.opExtrude","SWEPT_BODY",BODY,{"disambiguationData":[OSD([sQuery(id+"F8.wireOp",EDGE,"E7.0"),sQuery(id+"F8.wireOp",EDGE,"E10"),sQuery(id+"F8.wireOp",EDGE,"E11"),sQuery(id+"F8.wireOp",EDGE,"E12.1.0"),sQuery(id+"F8.wireOp",EDGE,"E12.1.1"),sQuery(id+"F8.wireOp",EDGE,"E12.2.0"),sQuery(id+"F8.wireOp",EDGE,"E12.2.1"),sQuery(id+"F8.wireOp",EDGE,"E12.3.0"),sQuery(id+"F8.wireOp",EDGE,"E12.3.1"),sQuery(id+"F8.wireOp",EDGE,"E12.4.0"),sQuery(id+"F8.wireOp",EDGE,"E12.4.1"),sQuery(id+"F8.wireOp",EDGE,"E12.5.0"),sQuery(id+"F8.wireOp",EDGE,"E12.5.1"),sQuery(id+"F8.wireOp",EDGE,"E12.6.0"),sQuery(id+"F8.wireOp",EDGE,"E13"),sQuery(id+"F8.wireOp",EDGE,"E14")])]}),"instanceName":"2"}),"instanceName":"2"});
            var Q4;
            Q4=sQuery(id+"F31.wireOp",EDGE,"E35");
            circularPattern(context, id + "F32", {"entities" : qUnion([Q0, Q1, Q2, Q3]), "axis" : qUnion([Q4]), "angle" : 72 * degree, "instanceCount" : round(3), "oppositeDirection" : true});
        }
        {
            var Q0;
            Q0=makeQuery(id+"F6.opPattern","COPY",FACE,{"derivedFrom":makeQuery(id+"F3.opExtrude","CAP_FACE",FACE,{"disambiguationData":[OSD([sQuery(id+"F1.wireOp",EDGE,"E2.0"),sQuery(id+"F1.wireOp",EDGE,"E2.1"),sQuery(id+"F1.wireOp",EDGE,"E2.2"),sQuery(id+"F1.wireOp",EDGE,"E2.3"),sQuery(id+"F1.wireOp",EDGE,"E2.4"),sQuery(id+"F1.wireOp",EDGE,"E2.5")])],"isStart":true}),"instanceName":"2"});
            var sketch = newSketch(context, id + "F33", { "sketchPlane" : qUnion([Q0])});
            skLineSegment(sketch, "E36", {"start": v(-4.1, 7.1) * mm, "end": v(-17.1, 29.6) * mm});
            skSolve(sketch);
        }
        {
            var Q0;
            Q0=sQuery(id+"F33.wireOp",VERTEX,"E36.end");
            var Q1;
            Q1=sQuery(id+"F33.wireOp",VERTEX,"E36.start");
            var Q2;
            Q2=sQuery(id+"F11.wireOp",VERTEX,"E16.end");
            cPlane(context, id + "F34", {"entities" : qUnion([Q0, Q1, Q2]), "cplaneType" : CPlaneType.THREE_POINT, "offset" : 150 * mm, "width" : 150 * mm, "height" : 150 * mm});
        }
        {
            var Q0;
            Q0=qCreatedBy(id+"F34.planeOp",FACE);
            var sketch = newSketch(context, id + "F35", { "sketchPlane" : qUnion([Q0])});
            skLineSegment(sketch, "E37.0", {"start": v(10.32, 0) * mm, "end": v(30.97, -15.77) * mm});
            skLineSegment(sketch, "E38", {"start": v(20.65, -7.89) * mm, "end": v(38.57, 15.58) * mm});
            skSolve(sketch);
        }
        {
            var Q0;
            Q0=makeQuery(id+"F2.opExtrude","SWEPT_BODY",BODY,{"disambiguationData":[OSD([sQuery(id+"F0.wireOp",EDGE,"E0.0"),sQuery(id+"F0.wireOp",EDGE,"E0.1"),sQuery(id+"F0.wireOp",EDGE,"E0.2"),sQuery(id+"F0.wireOp",EDGE,"E0.3"),sQuery(id+"F0.wireOp",EDGE,"E0.4")])]});
            var Q1;
            Q1=sQuery(id+"F35.wireOp",EDGE,"E38");
            circularPattern(context, id + "F36", {"entities" : qUnion([Q0]), "axis" : qUnion([Q1]), "angle" : 120 * degree, "instanceCount" : round(3), "oppositeDirection" : true});
        }
        {
            var Q0;
            Q0=makeQuery(id+"F36.opPattern","COPY",FACE,{"derivedFrom":makeQuery(id+"F2.opExtrude","CAP_FACE",FACE,{"disambiguationData":[OSD([sQuery(id+"F0.wireOp",EDGE,"E0.0"),sQuery(id+"F0.wireOp",EDGE,"E0.1"),sQuery(id+"F0.wireOp",EDGE,"E0.2"),sQuery(id+"F0.wireOp",EDGE,"E0.3"),sQuery(id+"F0.wireOp",EDGE,"E0.4")])],"isStart":true}),"instanceName":"1"});
            var sketch = newSketch(context, id + "F37", { "sketchPlane" : qUnion([Q0])});
            skLineSegment(sketch, "E39", {"start": v(-4.5, -30.9) * mm, "end": v(1.45, -42.2) * mm});
            skPoint(sketch, "E40.orphan", {"position": v(-9.3, -21.76) * mm});
            skSolve(sketch);
        }
        {
            var Q0;
            Q0=sQuery(id+"F37.wireOp",VERTEX,"E39.end");
            var Q1;
            Q1=sQuery(id+"F37.wireOp",VERTEX,"E39.start");
            var Q2;
            Q2=sQuery(id+"F35.wireOp",VERTEX,"E38.end");
            cPlane(context, id + "F38", {"entities" : qUnion([Q0, Q1, Q2]), "cplaneType" : CPlaneType.THREE_POINT, "offset" : 150 * mm, "width" : 150 * mm, "height" : 150 * mm});
        }
        {
            var Q0;
            Q0=qCreatedBy(id+"F38.planeOp",FACE);
            var sketch = newSketch(context, id + "F39", { "sketchPlane" : qUnion([Q0])});
            skLineSegment(sketch, "E41.0", {"start": v(29.7, -11.34) * mm, "end": v(36.4, -22.2) * mm});
            skLineSegment(sketch, "E42", {"start": v(29.7, -11.34) * mm, "end": v(58.3, 6.33) * mm});
            skSolve(sketch);
        }
        {
            var Q0;
            Q0=makeQuery(id+"F22.opPattern","COPY",BODY,{"derivedFrom":makeQuery(id+"F17.opPattern","COPY",BODY,{"derivedFrom":makeQuery(id+"F3.opExtrude","SWEPT_BODY",BODY,{"disambiguationData":[OSD([sQuery(id+"F1.wireOp",EDGE,"E2.0"),sQuery(id+"F1.wireOp",EDGE,"E2.1"),sQuery(id+"F1.wireOp",EDGE,"E2.2"),sQuery(id+"F1.wireOp",EDGE,"E2.3"),sQuery(id+"F1.wireOp",EDGE,"E2.4"),sQuery(id+"F1.wireOp",EDGE,"E2.5")])]}),"instanceName":"1"}),"instanceName":"2"});
            var Q1;
            Q1=makeQuery(id+"F22.opPattern","COPY",BODY,{"derivedFrom":makeQuery(id+"F17.opPattern","COPY",BODY,{"derivedFrom":makeQuery(id+"F16.opPattern","COPY",BODY,{"derivedFrom":makeQuery(id+"F15.opPattern","COPY",BODY,{"derivedFrom":makeQuery(id+"F9.opExtrude","SWEPT_BODY",BODY,{"disambiguationData":[OSD([sQuery(id+"F8.wireOp",EDGE,"E7.0"),sQuery(id+"F8.wireOp",EDGE,"E10"),sQuery(id+"F8.wireOp",EDGE,"E11"),sQuery(id+"F8.wireOp",EDGE,"E12.1.0"),sQuery(id+"F8.wireOp",EDGE,"E12.1.1"),sQuery(id+"F8.wireOp",EDGE,"E12.2.0"),sQuery(id+"F8.wireOp",EDGE,"E12.2.1"),sQuery(id+"F8.wireOp",EDGE,"E12.3.0"),sQuery(id+"F8.wireOp",EDGE,"E12.3.1"),sQuery(id+"F8.wireOp",EDGE,"E12.4.0"),sQuery(id+"F8.wireOp",EDGE,"E12.4.1"),sQuery(id+"F8.wireOp",EDGE,"E12.5.0"),sQuery(id+"F8.wireOp",EDGE,"E12.5.1"),sQuery(id+"F8.wireOp",EDGE,"E12.6.0"),sQuery(id+"F8.wireOp",EDGE,"E13"),sQuery(id+"F8.wireOp",EDGE,"E14")])]}),"instanceName":"2"}),"instanceName":"1"}),"instanceName":"1"}),"instanceName":"2"});
            var Q2;
            Q2=makeQuery(id+"F22.opPattern","COPY",BODY,{"derivedFrom":makeQuery(id+"F17.opPattern","COPY",BODY,{"derivedFrom":makeQuery(id+"F13.opPattern","COPY",BODY,{"derivedFrom":makeQuery(id+"F9.opExtrude","SWEPT_BODY",BODY,{"disambiguationData":[OSD([sQuery(id+"F8.wireOp",EDGE,"E7.0"),sQuery(id+"F8.wireOp",EDGE,"E10"),sQuery(id+"F8.wireOp",EDGE,"E11"),sQuery(id+"F8.wireOp",EDGE,"E12.1.0"),sQuery(id+"F8.wireOp",EDGE,"E12.1.1"),sQuery(id+"F8.wireOp",EDGE,"E12.2.0"),sQuery(id+"F8.wireOp",EDGE,"E12.2.1"),sQuery(id+"F8.wireOp",EDGE,"E12.3.0"),sQuery(id+"F8.wireOp",EDGE,"E12.3.1"),sQuery(id+"F8.wireOp",EDGE,"E12.4.0"),sQuery(id+"F8.wireOp",EDGE,"E12.4.1"),sQuery(id+"F8.wireOp",EDGE,"E12.5.0"),sQuery(id+"F8.wireOp",EDGE,"E12.5.1"),sQuery(id+"F8.wireOp",EDGE,"E12.6.0"),sQuery(id+"F8.wireOp",EDGE,"E13"),sQuery(id+"F8.wireOp",EDGE,"E14")])]}),"instanceName":"1"}),"instanceName":"1"}),"instanceName":"2"});
            var Q3;
            Q3=makeQuery(id+"F18.opPattern","COPY",BODY,{"derivedFrom":makeQuery(id+"F13.opPattern","COPY",BODY,{"derivedFrom":makeQuery(id+"F9.opExtrude","SWEPT_BODY",BODY,{"disambiguationData":[OSD([sQuery(id+"F8.wireOp",EDGE,"E7.0"),sQuery(id+"F8.wireOp",EDGE,"E10"),sQuery(id+"F8.wireOp",EDGE,"E11"),sQuery(id+"F8.wireOp",EDGE,"E12.1.0"),sQuery(id+"F8.wireOp",EDGE,"E12.1.1"),sQuery(id+"F8.wireOp",EDGE,"E12.2.0"),sQuery(id+"F8.wireOp",EDGE,"E12.2.1"),sQuery(id+"F8.wireOp",EDGE,"E12.3.0"),sQuery(id+"F8.wireOp",EDGE,"E12.3.1"),sQuery(id+"F8.wireOp",EDGE,"E12.4.0"),sQuery(id+"F8.wireOp",EDGE,"E12.4.1"),sQuery(id+"F8.wireOp",EDGE,"E12.5.0"),sQuery(id+"F8.wireOp",EDGE,"E12.5.1"),sQuery(id+"F8.wireOp",EDGE,"E12.6.0"),sQuery(id+"F8.wireOp",EDGE,"E13"),sQuery(id+"F8.wireOp",EDGE,"E14")])]}),"instanceName":"2"}),"instanceName":"1"});
            var Q4;
            Q4=sQuery(id+"F39.wireOp",EDGE,"E42");
            circularPattern(context, id + "F40", {"entities" : qUnion([Q0, Q1, Q2, Q3]), "axis" : qUnion([Q4]), "angle" : 72 * degree, "instanceCount" : round(3), "oppositeDirection" : true});
        }
        {
            var Q0;
            Q0=makeQuery(id+"F36.opPattern","COPY",FACE,{"derivedFrom":makeQuery(id+"F2.opExtrude","CAP_FACE",FACE,{"disambiguationData":[OSD([sQuery(id+"F0.wireOp",EDGE,"E0.0"),sQuery(id+"F0.wireOp",EDGE,"E0.1"),sQuery(id+"F0.wireOp",EDGE,"E0.2"),sQuery(id+"F0.wireOp",EDGE,"E0.3"),sQuery(id+"F0.wireOp",EDGE,"E0.4")])],"isStart":true}),"instanceName":"2"});
            var sketch = newSketch(context, id + "F41", { "sketchPlane" : qUnion([Q0])});
            skLineSegment(sketch, "E43", {"start": v(0, -18.47) * mm, "end": v(0, -31.23) * mm});
            skPoint(sketch, "E44.orphan", {"position": v(0, -41.55) * mm});
            skSolve(sketch);
        }
        {
            var Q0;
            Q0=sQuery(id+"F41.wireOp",VERTEX,"E43.end");
            var Q1;
            Q1=sQuery(id+"F41.wireOp",VERTEX,"E43.start");
            var Q2;
            Q2=sQuery(id+"F11.wireOp",VERTEX,"E16.end");
            cPlane(context, id + "F42", {"entities" : qUnion([Q0, Q1, Q2]), "cplaneType" : CPlaneType.THREE_POINT, "offset" : 150 * mm, "width" : 150 * mm, "height" : 150 * mm});
        }
        {
            var Q0;
            Q0=qCreatedBy(id+"F42.planeOp",FACE);
            var sketch = newSketch(context, id + "F43", { "sketchPlane" : qUnion([Q0])});
            skLineSegment(sketch, "E45.0", {"start": v(-25.52, -7.89) * mm, "end": v(-31.23, -19.3) * mm});
            skLineSegment(sketch, "E46", {"start": v(-31.23, -19.3) * mm, "end": v(-78.41, 4.3) * mm});
            skSolve(sketch);
        }
        {
            var Q0;
            Q0=makeQuery(id+"F40.opPattern","COPY",BODY,{"derivedFrom":makeQuery(id+"F22.opPattern","COPY",BODY,{"derivedFrom":makeQuery(id+"F17.opPattern","COPY",BODY,{"derivedFrom":makeQuery(id+"F3.opExtrude","SWEPT_BODY",BODY,{"disambiguationData":[OSD([sQuery(id+"F1.wireOp",EDGE,"E2.0"),sQuery(id+"F1.wireOp",EDGE,"E2.1"),sQuery(id+"F1.wireOp",EDGE,"E2.2"),sQuery(id+"F1.wireOp",EDGE,"E2.3"),sQuery(id+"F1.wireOp",EDGE,"E2.4"),sQuery(id+"F1.wireOp",EDGE,"E2.5")])]}),"instanceName":"1"}),"instanceName":"2"}),"instanceName":"2"});
            var Q1;
            Q1=makeQuery(id+"F40.opPattern","COPY",BODY,{"derivedFrom":makeQuery(id+"F22.opPattern","COPY",BODY,{"derivedFrom":makeQuery(id+"F17.opPattern","COPY",BODY,{"derivedFrom":makeQuery(id+"F13.opPattern","COPY",BODY,{"derivedFrom":makeQuery(id+"F9.opExtrude","SWEPT_BODY",BODY,{"disambiguationData":[OSD([sQuery(id+"F8.wireOp",EDGE,"E7.0"),sQuery(id+"F8.wireOp",EDGE,"E10"),sQuery(id+"F8.wireOp",EDGE,"E11"),sQuery(id+"F8.wireOp",EDGE,"E12.1.0"),sQuery(id+"F8.wireOp",EDGE,"E12.1.1"),sQuery(id+"F8.wireOp",EDGE,"E12.2.0"),sQuery(id+"F8.wireOp",EDGE,"E12.2.1"),sQuery(id+"F8.wireOp",EDGE,"E12.3.0"),sQuery(id+"F8.wireOp",EDGE,"E12.3.1"),sQuery(id+"F8.wireOp",EDGE,"E12.4.0"),sQuery(id+"F8.wireOp",EDGE,"E12.4.1"),sQuery(id+"F8.wireOp",EDGE,"E12.5.0"),sQuery(id+"F8.wireOp",EDGE,"E12.5.1"),sQuery(id+"F8.wireOp",EDGE,"E12.6.0"),sQuery(id+"F8.wireOp",EDGE,"E13"),sQuery(id+"F8.wireOp",EDGE,"E14")])]}),"instanceName":"1"}),"instanceName":"1"}),"instanceName":"2"}),"instanceName":"2"});
            var Q2;
            Q2=makeQuery(id+"F40.opPattern","COPY",BODY,{"derivedFrom":makeQuery(id+"F18.opPattern","COPY",BODY,{"derivedFrom":makeQuery(id+"F13.opPattern","COPY",BODY,{"derivedFrom":makeQuery(id+"F9.opExtrude","SWEPT_BODY",BODY,{"disambiguationData":[OSD([sQuery(id+"F8.wireOp",EDGE,"E7.0"),sQuery(id+"F8.wireOp",EDGE,"E10"),sQuery(id+"F8.wireOp",EDGE,"E11"),sQuery(id+"F8.wireOp",EDGE,"E12.1.0"),sQuery(id+"F8.wireOp",EDGE,"E12.1.1"),sQuery(id+"F8.wireOp",EDGE,"E12.2.0"),sQuery(id+"F8.wireOp",EDGE,"E12.2.1"),sQuery(id+"F8.wireOp",EDGE,"E12.3.0"),sQuery(id+"F8.wireOp",EDGE,"E12.3.1"),sQuery(id+"F8.wireOp",EDGE,"E12.4.0"),sQuery(id+"F8.wireOp",EDGE,"E12.4.1"),sQuery(id+"F8.wireOp",EDGE,"E12.5.0"),sQuery(id+"F8.wireOp",EDGE,"E12.5.1"),sQuery(id+"F8.wireOp",EDGE,"E12.6.0"),sQuery(id+"F8.wireOp",EDGE,"E13"),sQuery(id+"F8.wireOp",EDGE,"E14")])]}),"instanceName":"2"}),"instanceName":"1"}),"instanceName":"2"});
            var Q3;
            Q3=makeQuery(id+"F40.opPattern","COPY",BODY,{"derivedFrom":makeQuery(id+"F22.opPattern","COPY",BODY,{"derivedFrom":makeQuery(id+"F17.opPattern","COPY",BODY,{"derivedFrom":makeQuery(id+"F16.opPattern","COPY",BODY,{"derivedFrom":makeQuery(id+"F15.opPattern","COPY",BODY,{"derivedFrom":makeQuery(id+"F9.opExtrude","SWEPT_BODY",BODY,{"disambiguationData":[OSD([sQuery(id+"F8.wireOp",EDGE,"E7.0"),sQuery(id+"F8.wireOp",EDGE,"E10"),sQuery(id+"F8.wireOp",EDGE,"E11"),sQuery(id+"F8.wireOp",EDGE,"E12.1.0"),sQuery(id+"F8.wireOp",EDGE,"E12.1.1"),sQuery(id+"F8.wireOp",EDGE,"E12.2.0"),sQuery(id+"F8.wireOp",EDGE,"E12.2.1"),sQuery(id+"F8.wireOp",EDGE,"E12.3.0"),sQuery(id+"F8.wireOp",EDGE,"E12.3.1"),sQuery(id+"F8.wireOp",EDGE,"E12.4.0"),sQuery(id+"F8.wireOp",EDGE,"E12.4.1"),sQuery(id+"F8.wireOp",EDGE,"E12.5.0"),sQuery(id+"F8.wireOp",EDGE,"E12.5.1"),sQuery(id+"F8.wireOp",EDGE,"E12.6.0"),sQuery(id+"F8.wireOp",EDGE,"E13"),sQuery(id+"F8.wireOp",EDGE,"E14")])]}),"instanceName":"2"}),"instanceName":"1"}),"instanceName":"1"}),"instanceName":"2"}),"instanceName":"2"});
            var Q4;
            Q4=sQuery(id+"F43.wireOp",EDGE,"E46");
            circularPattern(context, id + "F44", {"entities" : qUnion([Q0, Q1, Q2, Q3]), "axis" : qUnion([Q4]), "angle" : 72 * degree, "instanceCount" : round(3), "oppositeDirection" : true});
        }
        {
            var Q0;
            Q0=makeQuery(id+"F40.opPattern","COPY",FACE,{"derivedFrom":makeQuery(id+"F22.opPattern","COPY",FACE,{"derivedFrom":makeQuery(id+"F17.opPattern","COPY",FACE,{"derivedFrom":makeQuery(id+"F3.opExtrude","CAP_FACE",FACE,{"disambiguationData":[OSD([sQuery(id+"F1.wireOp",EDGE,"E2.0"),sQuery(id+"F1.wireOp",EDGE,"E2.1"),sQuery(id+"F1.wireOp",EDGE,"E2.2"),sQuery(id+"F1.wireOp",EDGE,"E2.3"),sQuery(id+"F1.wireOp",EDGE,"E2.4"),sQuery(id+"F1.wireOp",EDGE,"E2.5")])],"isStart":true}),"instanceName":"1"}),"instanceName":"2"}),"instanceName":"1"});
            var sketch = newSketch(context, id + "F45", { "sketchPlane" : qUnion([Q0])});
            skLineSegment(sketch, "E47", {"start": v(1.3, -21.26) * mm, "end": v(2.09, -34.23) * mm});
            skSolve(sketch);
        }
        {
            var Q0;
            Q0=sQuery(id+"F45.wireOp",VERTEX,"E47.end");
            var Q1;
            Q1=sQuery(id+"F45.wireOp",VERTEX,"E47.start");
            var Q2;
            Q2=makeQuery(id+"F6.opPattern","COPY",VERTEX,{"derivedFrom":makeQuery(id+"F3.opExtrude","CAP_VERTEX",VERTEX,{"disambiguationData":[OSD([sQuery(id+"F1.wireOp",EDGE,"E2.1"),sQuery(id+"F1.wireOp",EDGE,"E2.2")])],"isStart":true}),"instanceName":"3"});
            cPlane(context, id + "F46", {"entities" : qUnion([Q0, Q1, Q2]), "cplaneType" : CPlaneType.THREE_POINT, "offset" : 150 * mm, "width" : 150 * mm, "height" : 150 * mm});
        }
        {
            var Q0;
            Q0=qCreatedBy(id+"F46.planeOp",FACE);
            var sketch = newSketch(context, id + "F47", { "sketchPlane" : qUnion([Q0])});
            skLineSegment(sketch, "E48.0", {"start": v(-35.84, -28.53) * mm, "end": v(-33.4, -41.3) * mm});
            skLineSegment(sketch, "E49", {"start": v(-33.4, -41.3) * mm, "end": v(-61.9, -46.73) * mm});
            skSolve(sketch);
        }
        {
            var Q0;
            Q0=makeQuery(id+"F22.opPattern","COPY",BODY,{"derivedFrom":makeQuery(id+"F17.opPattern","COPY",BODY,{"derivedFrom":makeQuery(id+"F3.opExtrude","SWEPT_BODY",BODY,{"disambiguationData":[OSD([sQuery(id+"F1.wireOp",EDGE,"E2.0"),sQuery(id+"F1.wireOp",EDGE,"E2.1"),sQuery(id+"F1.wireOp",EDGE,"E2.2"),sQuery(id+"F1.wireOp",EDGE,"E2.3"),sQuery(id+"F1.wireOp",EDGE,"E2.4"),sQuery(id+"F1.wireOp",EDGE,"E2.5")])]}),"instanceName":"1"}),"instanceName":"2"});
            var Q1;
            Q1=makeQuery(id+"F22.opPattern","COPY",BODY,{"derivedFrom":makeQuery(id+"F17.opPattern","COPY",BODY,{"derivedFrom":makeQuery(id+"F13.opPattern","COPY",BODY,{"derivedFrom":makeQuery(id+"F9.opExtrude","SWEPT_BODY",BODY,{"disambiguationData":[OSD([sQuery(id+"F8.wireOp",EDGE,"E7.0"),sQuery(id+"F8.wireOp",EDGE,"E10"),sQuery(id+"F8.wireOp",EDGE,"E11"),sQuery(id+"F8.wireOp",EDGE,"E12.1.0"),sQuery(id+"F8.wireOp",EDGE,"E12.1.1"),sQuery(id+"F8.wireOp",EDGE,"E12.2.0"),sQuery(id+"F8.wireOp",EDGE,"E12.2.1"),sQuery(id+"F8.wireOp",EDGE,"E12.3.0"),sQuery(id+"F8.wireOp",EDGE,"E12.3.1"),sQuery(id+"F8.wireOp",EDGE,"E12.4.0"),sQuery(id+"F8.wireOp",EDGE,"E12.4.1"),sQuery(id+"F8.wireOp",EDGE,"E12.5.0"),sQuery(id+"F8.wireOp",EDGE,"E12.5.1"),sQuery(id+"F8.wireOp",EDGE,"E12.6.0"),sQuery(id+"F8.wireOp",EDGE,"E13"),sQuery(id+"F8.wireOp",EDGE,"E14")])]}),"instanceName":"1"}),"instanceName":"1"}),"instanceName":"2"});
            var Q2;
            Q2=makeQuery(id+"F22.opPattern","COPY",BODY,{"derivedFrom":makeQuery(id+"F17.opPattern","COPY",BODY,{"derivedFrom":makeQuery(id+"F16.opPattern","COPY",BODY,{"derivedFrom":makeQuery(id+"F15.opPattern","COPY",BODY,{"derivedFrom":makeQuery(id+"F9.opExtrude","SWEPT_BODY",BODY,{"disambiguationData":[OSD([sQuery(id+"F8.wireOp",EDGE,"E7.0"),sQuery(id+"F8.wireOp",EDGE,"E10"),sQuery(id+"F8.wireOp",EDGE,"E11"),sQuery(id+"F8.wireOp",EDGE,"E12.1.0"),sQuery(id+"F8.wireOp",EDGE,"E12.1.1"),sQuery(id+"F8.wireOp",EDGE,"E12.2.0"),sQuery(id+"F8.wireOp",EDGE,"E12.2.1"),sQuery(id+"F8.wireOp",EDGE,"E12.3.0"),sQuery(id+"F8.wireOp",EDGE,"E12.3.1"),sQuery(id+"F8.wireOp",EDGE,"E12.4.0"),sQuery(id+"F8.wireOp",EDGE,"E12.4.1"),sQuery(id+"F8.wireOp",EDGE,"E12.5.0"),sQuery(id+"F8.wireOp",EDGE,"E12.5.1"),sQuery(id+"F8.wireOp",EDGE,"E12.6.0"),sQuery(id+"F8.wireOp",EDGE,"E13"),sQuery(id+"F8.wireOp",EDGE,"E14")])]}),"instanceName":"2"}),"instanceName":"1"}),"instanceName":"1"}),"instanceName":"2"});
            var Q3;
            Q3=makeQuery(id+"F18.opPattern","COPY",BODY,{"derivedFrom":makeQuery(id+"F13.opPattern","COPY",BODY,{"derivedFrom":makeQuery(id+"F9.opExtrude","SWEPT_BODY",BODY,{"disambiguationData":[OSD([sQuery(id+"F8.wireOp",EDGE,"E7.0"),sQuery(id+"F8.wireOp",EDGE,"E10"),sQuery(id+"F8.wireOp",EDGE,"E11"),sQuery(id+"F8.wireOp",EDGE,"E12.1.0"),sQuery(id+"F8.wireOp",EDGE,"E12.1.1"),sQuery(id+"F8.wireOp",EDGE,"E12.2.0"),sQuery(id+"F8.wireOp",EDGE,"E12.2.1"),sQuery(id+"F8.wireOp",EDGE,"E12.3.0"),sQuery(id+"F8.wireOp",EDGE,"E12.3.1"),sQuery(id+"F8.wireOp",EDGE,"E12.4.0"),sQuery(id+"F8.wireOp",EDGE,"E12.4.1"),sQuery(id+"F8.wireOp",EDGE,"E12.5.0"),sQuery(id+"F8.wireOp",EDGE,"E12.5.1"),sQuery(id+"F8.wireOp",EDGE,"E12.6.0"),sQuery(id+"F8.wireOp",EDGE,"E13"),sQuery(id+"F8.wireOp",EDGE,"E14")])]}),"instanceName":"2"}),"instanceName":"1"});
            var Q4;
            Q4=sQuery(id+"F47.wireOp",EDGE,"E49");
            circularPattern(context, id + "F48", {"entities" : qUnion([Q0, Q1, Q2, Q3]), "axis" : qUnion([Q4]), "angle" : 120 * degree, "instanceCount" : 2, "oppositeDirection" : true});
        }
        {
            var Q0;
            Q0=makeQuery(id+"F26.opPattern","COPY",FACE,{"derivedFrom":makeQuery(id+"F3.opExtrude","CAP_FACE",FACE,{"disambiguationData":[OSD([sQuery(id+"F1.wireOp",EDGE,"E2.0"),sQuery(id+"F1.wireOp",EDGE,"E2.1"),sQuery(id+"F1.wireOp",EDGE,"E2.2"),sQuery(id+"F1.wireOp",EDGE,"E2.3"),sQuery(id+"F1.wireOp",EDGE,"E2.4"),sQuery(id+"F1.wireOp",EDGE,"E2.5")])],"isStart":true}),"instanceName":"1"});
            var sketch = newSketch(context, id + "F49", { "sketchPlane" : qUnion([Q0])});
            skLineSegment(sketch, "E50", {"start": v(-12.92, -27.06) * mm, "end": v(-2.09, -34.23) * mm});
            skSolve(sketch);
        }
        {
            var Q0;
            Q0=sQuery(id+"F49.wireOp",VERTEX,"E50.end");
            var Q1;
            Q1=sQuery(id+"F49.wireOp",VERTEX,"E50.start");
            var Q2;
            Q2=makeQuery(id+"F6.opPattern","COPY",VERTEX,{"derivedFrom":makeQuery(id+"F3.opExtrude","CAP_VERTEX",VERTEX,{"disambiguationData":[OSD([sQuery(id+"F1.wireOp",EDGE,"E2.0"),sQuery(id+"F1.wireOp",EDGE,"E2.5")])],"isStart":true}),"instanceName":"4"});
            cPlane(context, id + "F50", {"entities" : qUnion([Q0, Q1, Q2]), "cplaneType" : CPlaneType.THREE_POINT, "offset" : 150 * mm, "width" : 150 * mm, "height" : 150 * mm});
        }
        {
            var Q0;
            Q0=qCreatedBy(id+"F50.planeOp",FACE);
            var sketch = newSketch(context, id + "F51", { "sketchPlane" : qUnion([Q0])});
            skLineSegment(sketch, "E51.0", {"start": v(27.14, -5.92) * mm, "end": v(31.77, 6.22) * mm});
            skLineSegment(sketch, "E52", {"start": v(31.77, 6.22) * mm, "end": v(70.56, -8.6) * mm});
            skSolve(sketch);
        }
        {
            var Q0;
            Q0=makeQuery(id+"F16.opPattern","COPY",BODY,{"derivedFrom":makeQuery(id+"F15.opPattern","COPY",BODY,{"derivedFrom":makeQuery(id+"F9.opExtrude","SWEPT_BODY",BODY,{"disambiguationData":[OSD([sQuery(id+"F8.wireOp",EDGE,"E7.0"),sQuery(id+"F8.wireOp",EDGE,"E10"),sQuery(id+"F8.wireOp",EDGE,"E11"),sQuery(id+"F8.wireOp",EDGE,"E12.1.0"),sQuery(id+"F8.wireOp",EDGE,"E12.1.1"),sQuery(id+"F8.wireOp",EDGE,"E12.2.0"),sQuery(id+"F8.wireOp",EDGE,"E12.2.1"),sQuery(id+"F8.wireOp",EDGE,"E12.3.0"),sQuery(id+"F8.wireOp",EDGE,"E12.3.1"),sQuery(id+"F8.wireOp",EDGE,"E12.4.0"),sQuery(id+"F8.wireOp",EDGE,"E12.4.1"),sQuery(id+"F8.wireOp",EDGE,"E12.5.0"),sQuery(id+"F8.wireOp",EDGE,"E12.5.1"),sQuery(id+"F8.wireOp",EDGE,"E12.6.0"),sQuery(id+"F8.wireOp",EDGE,"E13"),sQuery(id+"F8.wireOp",EDGE,"E14")])]}),"instanceName":"1"}),"instanceName":"1"});
            var Q1;
            Q1=makeQuery(id+"F13.opPattern","COPY",BODY,{"derivedFrom":makeQuery(id+"F9.opExtrude","SWEPT_BODY",BODY,{"disambiguationData":[OSD([sQuery(id+"F8.wireOp",EDGE,"E7.0"),sQuery(id+"F8.wireOp",EDGE,"E10"),sQuery(id+"F8.wireOp",EDGE,"E11"),sQuery(id+"F8.wireOp",EDGE,"E12.1.0"),sQuery(id+"F8.wireOp",EDGE,"E12.1.1"),sQuery(id+"F8.wireOp",EDGE,"E12.2.0"),sQuery(id+"F8.wireOp",EDGE,"E12.2.1"),sQuery(id+"F8.wireOp",EDGE,"E12.3.0"),sQuery(id+"F8.wireOp",EDGE,"E12.3.1"),sQuery(id+"F8.wireOp",EDGE,"E12.4.0"),sQuery(id+"F8.wireOp",EDGE,"E12.4.1"),sQuery(id+"F8.wireOp",EDGE,"E12.5.0"),sQuery(id+"F8.wireOp",EDGE,"E12.5.1"),sQuery(id+"F8.wireOp",EDGE,"E12.6.0"),sQuery(id+"F8.wireOp",EDGE,"E13"),sQuery(id+"F8.wireOp",EDGE,"E14")])]}),"instanceName":"1"});
            var Q2;
            Q2=makeQuery(id+"F16.opPattern","COPY",BODY,{"derivedFrom":makeQuery(id+"F15.opPattern","COPY",BODY,{"derivedFrom":makeQuery(id+"F9.opExtrude","SWEPT_BODY",BODY,{"disambiguationData":[OSD([sQuery(id+"F8.wireOp",EDGE,"E7.0"),sQuery(id+"F8.wireOp",EDGE,"E10"),sQuery(id+"F8.wireOp",EDGE,"E11"),sQuery(id+"F8.wireOp",EDGE,"E12.1.0"),sQuery(id+"F8.wireOp",EDGE,"E12.1.1"),sQuery(id+"F8.wireOp",EDGE,"E12.2.0"),sQuery(id+"F8.wireOp",EDGE,"E12.2.1"),sQuery(id+"F8.wireOp",EDGE,"E12.3.0"),sQuery(id+"F8.wireOp",EDGE,"E12.3.1"),sQuery(id+"F8.wireOp",EDGE,"E12.4.0"),sQuery(id+"F8.wireOp",EDGE,"E12.4.1"),sQuery(id+"F8.wireOp",EDGE,"E12.5.0"),sQuery(id+"F8.wireOp",EDGE,"E12.5.1"),sQuery(id+"F8.wireOp",EDGE,"E12.6.0"),sQuery(id+"F8.wireOp",EDGE,"E13"),sQuery(id+"F8.wireOp",EDGE,"E14")])]}),"instanceName":"2"}),"instanceName":"1"});
            var Q3;
            Q3=makeQuery(id+"F3.opExtrude","SWEPT_BODY",BODY,{"disambiguationData":[OSD([sQuery(id+"F1.wireOp",EDGE,"E2.0"),sQuery(id+"F1.wireOp",EDGE,"E2.1"),sQuery(id+"F1.wireOp",EDGE,"E2.2"),sQuery(id+"F1.wireOp",EDGE,"E2.3"),sQuery(id+"F1.wireOp",EDGE,"E2.4"),sQuery(id+"F1.wireOp",EDGE,"E2.5")])]});
            var Q4;
            Q4=sQuery(id+"F51.wireOp",EDGE,"E52");
            circularPattern(context, id + "F52", {"entities" : qUnion([Q0, Q1, Q2, Q3]), "axis" : qUnion([Q4]), "angle" : 120 * degree, "instanceCount" : round(2), "oppositeDirection" : true});
        }
        {
            var Q0;
            Q0=makeQuery(id+"F32.opPattern","COPY",FACE,{"derivedFrom":makeQuery(id+"F26.opPattern","COPY",FACE,{"derivedFrom":makeQuery(id+"F3.opExtrude","CAP_FACE",FACE,{"disambiguationData":[OSD([sQuery(id+"F1.wireOp",EDGE,"E2.0"),sQuery(id+"F1.wireOp",EDGE,"E2.1"),sQuery(id+"F1.wireOp",EDGE,"E2.2"),sQuery(id+"F1.wireOp",EDGE,"E2.3"),sQuery(id+"F1.wireOp",EDGE,"E2.4"),sQuery(id+"F1.wireOp",EDGE,"E2.5")])],"isStart":true}),"instanceName":"2"}),"instanceName":"1"});
            var sketch = newSketch(context, id + "F53", { "sketchPlane" : qUnion([Q0])});
            skLineSegment(sketch, "E53", {"start": v(-10.6, -33.35) * mm, "end": v(-10.6, -18.35) * mm});
            skSolve(sketch);
        }
        {
            var Q0;
            Q0=sQuery(id+"F53.wireOp",VERTEX,"E53.start");
            var Q1;
            Q1=sQuery(id+"F53.wireOp",VERTEX,"E53.end");
            var Q2;
            Q2=makeQuery(id+"F32.opPattern","COPY",VERTEX,{"derivedFrom":makeQuery(id+"F26.opPattern","COPY",VERTEX,{"derivedFrom":makeQuery(id+"F3.opExtrude","CAP_VERTEX",VERTEX,{"disambiguationData":[OSD([sQuery(id+"F1.wireOp",EDGE,"E2.2"),sQuery(id+"F1.wireOp",EDGE,"E2.3")])],"isStart":false}),"instanceName":"2"}),"instanceName":"1"});
            cPlane(context, id + "F54", {"entities" : qUnion([Q0, Q1, Q2]), "cplaneType" : CPlaneType.THREE_POINT, "offset" : 150 * mm, "width" : 150 * mm, "height" : 150 * mm});
        }
        {
            var Q0;
            Q0=qCreatedBy(id+"F54.planeOp",FACE);
            var sketch = newSketch(context, id + "F55", { "sketchPlane" : qUnion([Q0])});
            skLineSegment(sketch, "E54.0", {"start": v(-2, -70.16) * mm, "end": v(-14.98, -62.66) * mm});
            skLineSegment(sketch, "E55", {"start": v(-14.98, -62.66) * mm, "end": v(-37.7, -102) * mm});
            skSolve(sketch);
        }
        {
            var Q0;
            Q0=makeQuery(id+"F26.opPattern","COPY",BODY,{"derivedFrom":makeQuery(id+"F3.opExtrude","SWEPT_BODY",BODY,{"disambiguationData":[OSD([sQuery(id+"F1.wireOp",EDGE,"E2.0"),sQuery(id+"F1.wireOp",EDGE,"E2.1"),sQuery(id+"F1.wireOp",EDGE,"E2.2"),sQuery(id+"F1.wireOp",EDGE,"E2.3"),sQuery(id+"F1.wireOp",EDGE,"E2.4"),sQuery(id+"F1.wireOp",EDGE,"E2.5")])]}),"instanceName":"2"});
            var Q1;
            Q1=makeQuery(id+"F26.opPattern","COPY",BODY,{"derivedFrom":makeQuery(id+"F16.opPattern","COPY",BODY,{"derivedFrom":makeQuery(id+"F15.opPattern","COPY",BODY,{"derivedFrom":makeQuery(id+"F9.opExtrude","SWEPT_BODY",BODY,{"disambiguationData":[OSD([sQuery(id+"F8.wireOp",EDGE,"E7.0"),sQuery(id+"F8.wireOp",EDGE,"E10"),sQuery(id+"F8.wireOp",EDGE,"E11"),sQuery(id+"F8.wireOp",EDGE,"E12.1.0"),sQuery(id+"F8.wireOp",EDGE,"E12.1.1"),sQuery(id+"F8.wireOp",EDGE,"E12.2.0"),sQuery(id+"F8.wireOp",EDGE,"E12.2.1"),sQuery(id+"F8.wireOp",EDGE,"E12.3.0"),sQuery(id+"F8.wireOp",EDGE,"E12.3.1"),sQuery(id+"F8.wireOp",EDGE,"E12.4.0"),sQuery(id+"F8.wireOp",EDGE,"E12.4.1"),sQuery(id+"F8.wireOp",EDGE,"E12.5.0"),sQuery(id+"F8.wireOp",EDGE,"E12.5.1"),sQuery(id+"F8.wireOp",EDGE,"E12.6.0"),sQuery(id+"F8.wireOp",EDGE,"E13"),sQuery(id+"F8.wireOp",EDGE,"E14")])]}),"instanceName":"2"}),"instanceName":"1"}),"instanceName":"2"});
            var Q2;
            Q2=makeQuery(id+"F26.opPattern","COPY",BODY,{"derivedFrom":makeQuery(id+"F13.opPattern","COPY",BODY,{"derivedFrom":makeQuery(id+"F9.opExtrude","SWEPT_BODY",BODY,{"disambiguationData":[OSD([sQuery(id+"F8.wireOp",EDGE,"E7.0"),sQuery(id+"F8.wireOp",EDGE,"E10"),sQuery(id+"F8.wireOp",EDGE,"E11"),sQuery(id+"F8.wireOp",EDGE,"E12.1.0"),sQuery(id+"F8.wireOp",EDGE,"E12.1.1"),sQuery(id+"F8.wireOp",EDGE,"E12.2.0"),sQuery(id+"F8.wireOp",EDGE,"E12.2.1"),sQuery(id+"F8.wireOp",EDGE,"E12.3.0"),sQuery(id+"F8.wireOp",EDGE,"E12.3.1"),sQuery(id+"F8.wireOp",EDGE,"E12.4.0"),sQuery(id+"F8.wireOp",EDGE,"E12.4.1"),sQuery(id+"F8.wireOp",EDGE,"E12.5.0"),sQuery(id+"F8.wireOp",EDGE,"E12.5.1"),sQuery(id+"F8.wireOp",EDGE,"E12.6.0"),sQuery(id+"F8.wireOp",EDGE,"E13"),sQuery(id+"F8.wireOp",EDGE,"E14")])]}),"instanceName":"1"}),"instanceName":"2"});
            var Q3;
            Q3=makeQuery(id+"F18.opPattern","COPY",BODY,{"derivedFrom":makeQuery(id+"F13.opPattern","COPY",BODY,{"derivedFrom":makeQuery(id+"F9.opExtrude","SWEPT_BODY",BODY,{"disambiguationData":[OSD([sQuery(id+"F8.wireOp",EDGE,"E7.0"),sQuery(id+"F8.wireOp",EDGE,"E10"),sQuery(id+"F8.wireOp",EDGE,"E11"),sQuery(id+"F8.wireOp",EDGE,"E12.1.0"),sQuery(id+"F8.wireOp",EDGE,"E12.1.1"),sQuery(id+"F8.wireOp",EDGE,"E12.2.0"),sQuery(id+"F8.wireOp",EDGE,"E12.2.1"),sQuery(id+"F8.wireOp",EDGE,"E12.3.0"),sQuery(id+"F8.wireOp",EDGE,"E12.3.1"),sQuery(id+"F8.wireOp",EDGE,"E12.4.0"),sQuery(id+"F8.wireOp",EDGE,"E12.4.1"),sQuery(id+"F8.wireOp",EDGE,"E12.5.0"),sQuery(id+"F8.wireOp",EDGE,"E12.5.1"),sQuery(id+"F8.wireOp",EDGE,"E12.6.0"),sQuery(id+"F8.wireOp",EDGE,"E13"),sQuery(id+"F8.wireOp",EDGE,"E14")])]}),"instanceName":"2"}),"instanceName":"2"});
            var Q4;
            Q4=sQuery(id+"F55.wireOp",EDGE,"E55");
            circularPattern(context, id + "F56", {"entities" : qUnion([Q0, Q1, Q2, Q3]), "axis" : qUnion([Q4]), "angle" : 120 * degree, "instanceCount" : 2, "oppositeDirection" : true});
        }
        {
            var Q0;
            Q0=makeQuery(id+"F56.opPattern","COPY",FACE,{"derivedFrom":makeQuery(id+"F26.opPattern","COPY",FACE,{"derivedFrom":makeQuery(id+"F3.opExtrude","CAP_FACE",FACE,{"disambiguationData":[OSD([sQuery(id+"F1.wireOp",EDGE,"E2.0"),sQuery(id+"F1.wireOp",EDGE,"E2.1"),sQuery(id+"F1.wireOp",EDGE,"E2.2"),sQuery(id+"F1.wireOp",EDGE,"E2.3"),sQuery(id+"F1.wireOp",EDGE,"E2.4"),sQuery(id+"F1.wireOp",EDGE,"E2.5")])],"isStart":true}),"instanceName":"2"}),"instanceName":"1"});
            var sketch = newSketch(context, id + "F57", { "sketchPlane" : qUnion([Q0])});
            skLineSegment(sketch, "E56", {"start": v(-34.48, 6) * mm, "end": v(-19.62, 8.02) * mm});
            skSolve(sketch);
        }
        {
            var Q0;
            Q0=sQuery(id+"F57.wireOp",VERTEX,"E56.start");
            var Q1;
            Q1=sQuery(id+"F57.wireOp",VERTEX,"E56.end");
            var Q2;
            Q2=makeQuery(id+"F56.opPattern","COPY",VERTEX,{"derivedFrom":makeQuery(id+"F26.opPattern","COPY",VERTEX,{"derivedFrom":makeQuery(id+"F3.opExtrude","CAP_VERTEX",VERTEX,{"disambiguationData":[OSD([sQuery(id+"F1.wireOp",EDGE,"E2.2"),sQuery(id+"F1.wireOp",EDGE,"E2.3")])],"isStart":false}),"instanceName":"2"}),"instanceName":"1"});
            cPlane(context, id + "F58", {"entities" : qUnion([Q0, Q1, Q2]), "cplaneType" : CPlaneType.THREE_POINT, "offset" : 150 * mm, "width" : 150 * mm, "height" : 150 * mm});
        }
        {
            var Q0;
            Q0=qCreatedBy(id+"F58.planeOp",FACE);
            var sketch = newSketch(context, id + "F59", { "sketchPlane" : qUnion([Q0])});
            skLineSegment(sketch, "E57.0", {"start": v(-8.72, -69.64) * mm, "end": v(-20.93, -60.93) * mm});
            skLineSegment(sketch, "E58", {"start": v(-20.93, -60.93) * mm, "end": v(-30.12, -73.8) * mm});
            skSolve(sketch);
        }
        {
            var Q0;
            Q0=makeQuery(id+"F52.opPattern","COPY",BODY,{"derivedFrom":makeQuery(id+"F3.opExtrude","SWEPT_BODY",BODY,{"disambiguationData":[OSD([sQuery(id+"F1.wireOp",EDGE,"E2.0"),sQuery(id+"F1.wireOp",EDGE,"E2.1"),sQuery(id+"F1.wireOp",EDGE,"E2.2"),sQuery(id+"F1.wireOp",EDGE,"E2.3"),sQuery(id+"F1.wireOp",EDGE,"E2.4"),sQuery(id+"F1.wireOp",EDGE,"E2.5")])]}),"instanceName":"1"});
            var Q1;
            Q1=makeQuery(id+"F52.opPattern","COPY",BODY,{"derivedFrom":makeQuery(id+"F16.opPattern","COPY",BODY,{"derivedFrom":makeQuery(id+"F15.opPattern","COPY",BODY,{"derivedFrom":makeQuery(id+"F9.opExtrude","SWEPT_BODY",BODY,{"disambiguationData":[OSD([sQuery(id+"F8.wireOp",EDGE,"E7.0"),sQuery(id+"F8.wireOp",EDGE,"E10"),sQuery(id+"F8.wireOp",EDGE,"E11"),sQuery(id+"F8.wireOp",EDGE,"E12.1.0"),sQuery(id+"F8.wireOp",EDGE,"E12.1.1"),sQuery(id+"F8.wireOp",EDGE,"E12.2.0"),sQuery(id+"F8.wireOp",EDGE,"E12.2.1"),sQuery(id+"F8.wireOp",EDGE,"E12.3.0"),sQuery(id+"F8.wireOp",EDGE,"E12.3.1"),sQuery(id+"F8.wireOp",EDGE,"E12.4.0"),sQuery(id+"F8.wireOp",EDGE,"E12.4.1"),sQuery(id+"F8.wireOp",EDGE,"E12.5.0"),sQuery(id+"F8.wireOp",EDGE,"E12.5.1"),sQuery(id+"F8.wireOp",EDGE,"E12.6.0"),sQuery(id+"F8.wireOp",EDGE,"E13"),sQuery(id+"F8.wireOp",EDGE,"E14")])]}),"instanceName":"2"}),"instanceName":"1"}),"instanceName":"1"});
            var Q2;
            Q2=makeQuery(id+"F52.opPattern","COPY",BODY,{"derivedFrom":makeQuery(id+"F16.opPattern","COPY",BODY,{"derivedFrom":makeQuery(id+"F15.opPattern","COPY",BODY,{"derivedFrom":makeQuery(id+"F9.opExtrude","SWEPT_BODY",BODY,{"disambiguationData":[OSD([sQuery(id+"F8.wireOp",EDGE,"E7.0"),sQuery(id+"F8.wireOp",EDGE,"E10"),sQuery(id+"F8.wireOp",EDGE,"E11"),sQuery(id+"F8.wireOp",EDGE,"E12.1.0"),sQuery(id+"F8.wireOp",EDGE,"E12.1.1"),sQuery(id+"F8.wireOp",EDGE,"E12.2.0"),sQuery(id+"F8.wireOp",EDGE,"E12.2.1"),sQuery(id+"F8.wireOp",EDGE,"E12.3.0"),sQuery(id+"F8.wireOp",EDGE,"E12.3.1"),sQuery(id+"F8.wireOp",EDGE,"E12.4.0"),sQuery(id+"F8.wireOp",EDGE,"E12.4.1"),sQuery(id+"F8.wireOp",EDGE,"E12.5.0"),sQuery(id+"F8.wireOp",EDGE,"E12.5.1"),sQuery(id+"F8.wireOp",EDGE,"E12.6.0"),sQuery(id+"F8.wireOp",EDGE,"E13"),sQuery(id+"F8.wireOp",EDGE,"E14")])]}),"instanceName":"1"}),"instanceName":"1"}),"instanceName":"1"});
            var Q3;
            Q3=makeQuery(id+"F52.opPattern","COPY",BODY,{"derivedFrom":makeQuery(id+"F13.opPattern","COPY",BODY,{"derivedFrom":makeQuery(id+"F9.opExtrude","SWEPT_BODY",BODY,{"disambiguationData":[OSD([sQuery(id+"F8.wireOp",EDGE,"E7.0"),sQuery(id+"F8.wireOp",EDGE,"E10"),sQuery(id+"F8.wireOp",EDGE,"E11"),sQuery(id+"F8.wireOp",EDGE,"E12.1.0"),sQuery(id+"F8.wireOp",EDGE,"E12.1.1"),sQuery(id+"F8.wireOp",EDGE,"E12.2.0"),sQuery(id+"F8.wireOp",EDGE,"E12.2.1"),sQuery(id+"F8.wireOp",EDGE,"E12.3.0"),sQuery(id+"F8.wireOp",EDGE,"E12.3.1"),sQuery(id+"F8.wireOp",EDGE,"E12.4.0"),sQuery(id+"F8.wireOp",EDGE,"E12.4.1"),sQuery(id+"F8.wireOp",EDGE,"E12.5.0"),sQuery(id+"F8.wireOp",EDGE,"E12.5.1"),sQuery(id+"F8.wireOp",EDGE,"E12.6.0"),sQuery(id+"F8.wireOp",EDGE,"E13"),sQuery(id+"F8.wireOp",EDGE,"E14")])]}),"instanceName":"1"}),"instanceName":"1"});
            var Q4;
            Q4=sQuery(id+"F59.wireOp",EDGE,"E58");
            circularPattern(context, id + "F60", {"entities" : qUnion([Q0, Q1, Q2, Q3]), "axis" : qUnion([Q4]), "angle" : 120 * degree, "instanceCount" : 2, "oppositeDirection" : true});
        }
        {
            var Q0;
            Q0=makeQuery(id+"F22.opPattern","COPY",BODY,{"derivedFrom":makeQuery(id+"F17.opPattern","COPY",BODY,{"derivedFrom":makeQuery(id+"F16.opPattern","COPY",BODY,{"derivedFrom":makeQuery(id+"F15.opPattern","COPY",BODY,{"derivedFrom":makeQuery(id+"F9.opExtrude","SWEPT_BODY",BODY,{"disambiguationData":[OSD([sQuery(id+"F8.wireOp",EDGE,"E7.0"),sQuery(id+"F8.wireOp",EDGE,"E10"),sQuery(id+"F8.wireOp",EDGE,"E11"),sQuery(id+"F8.wireOp",EDGE,"E12.1.0"),sQuery(id+"F8.wireOp",EDGE,"E12.1.1"),sQuery(id+"F8.wireOp",EDGE,"E12.2.0"),sQuery(id+"F8.wireOp",EDGE,"E12.2.1"),sQuery(id+"F8.wireOp",EDGE,"E12.3.0"),sQuery(id+"F8.wireOp",EDGE,"E12.3.1"),sQuery(id+"F8.wireOp",EDGE,"E12.4.0"),sQuery(id+"F8.wireOp",EDGE,"E12.4.1"),sQuery(id+"F8.wireOp",EDGE,"E12.5.0"),sQuery(id+"F8.wireOp",EDGE,"E12.5.1"),sQuery(id+"F8.wireOp",EDGE,"E12.6.0"),sQuery(id+"F8.wireOp",EDGE,"E13"),sQuery(id+"F8.wireOp",EDGE,"E14")])]}),"instanceName":"1"}),"instanceName":"1"}),"instanceName":"1"}),"instanceName":"1"});
            deleteBodies(context, id + "F61", {"entities" : qUnion([Q0])});
        }
        {
            var Q0;
            Q0=makeQuery(id+"F22.opPattern","COPY",BODY,{"derivedFrom":makeQuery(id+"F17.opPattern","COPY",BODY,{"derivedFrom":makeQuery(id+"F16.opPattern","COPY",BODY,{"derivedFrom":makeQuery(id+"F15.opPattern","COPY",BODY,{"derivedFrom":makeQuery(id+"F9.opExtrude","SWEPT_BODY",BODY,{"disambiguationData":[OSD([sQuery(id+"F8.wireOp",EDGE,"E7.0"),sQuery(id+"F8.wireOp",EDGE,"E10"),sQuery(id+"F8.wireOp",EDGE,"E11"),sQuery(id+"F8.wireOp",EDGE,"E12.1.0"),sQuery(id+"F8.wireOp",EDGE,"E12.1.1"),sQuery(id+"F8.wireOp",EDGE,"E12.2.0"),sQuery(id+"F8.wireOp",EDGE,"E12.2.1"),sQuery(id+"F8.wireOp",EDGE,"E12.3.0"),sQuery(id+"F8.wireOp",EDGE,"E12.3.1"),sQuery(id+"F8.wireOp",EDGE,"E12.4.0"),sQuery(id+"F8.wireOp",EDGE,"E12.4.1"),sQuery(id+"F8.wireOp",EDGE,"E12.5.0"),sQuery(id+"F8.wireOp",EDGE,"E12.5.1"),sQuery(id+"F8.wireOp",EDGE,"E12.6.0"),sQuery(id+"F8.wireOp",EDGE,"E13"),sQuery(id+"F8.wireOp",EDGE,"E14")])]}),"instanceName":"1"}),"instanceName":"1"}),"instanceName":"1"}),"instanceName":"2"});
            deleteBodies(context, id + "F62", {"entities" : qUnion([Q0])});
        }
        {
            var Q0;
            Q0=makeQuery(id+"F26.opPattern","COPY",BODY,{"derivedFrom":makeQuery(id+"F16.opPattern","COPY",BODY,{"derivedFrom":makeQuery(id+"F15.opPattern","COPY",BODY,{"derivedFrom":makeQuery(id+"F9.opExtrude","SWEPT_BODY",BODY,{"disambiguationData":[OSD([sQuery(id+"F8.wireOp",EDGE,"E7.0"),sQuery(id+"F8.wireOp",EDGE,"E10"),sQuery(id+"F8.wireOp",EDGE,"E11"),sQuery(id+"F8.wireOp",EDGE,"E12.1.0"),sQuery(id+"F8.wireOp",EDGE,"E12.1.1"),sQuery(id+"F8.wireOp",EDGE,"E12.2.0"),sQuery(id+"F8.wireOp",EDGE,"E12.2.1"),sQuery(id+"F8.wireOp",EDGE,"E12.3.0"),sQuery(id+"F8.wireOp",EDGE,"E12.3.1"),sQuery(id+"F8.wireOp",EDGE,"E12.4.0"),sQuery(id+"F8.wireOp",EDGE,"E12.4.1"),sQuery(id+"F8.wireOp",EDGE,"E12.5.0"),sQuery(id+"F8.wireOp",EDGE,"E12.5.1"),sQuery(id+"F8.wireOp",EDGE,"E12.6.0"),sQuery(id+"F8.wireOp",EDGE,"E13"),sQuery(id+"F8.wireOp",EDGE,"E14")])]}),"instanceName":"1"}),"instanceName":"1"}),"instanceName":"1"});
            deleteBodies(context, id + "F63", {"entities" : qUnion([Q0])});
        }
        {
            var Q0;
            Q0=makeQuery(id+"F26.opPattern","COPY",BODY,{"derivedFrom":makeQuery(id+"F16.opPattern","COPY",BODY,{"derivedFrom":makeQuery(id+"F15.opPattern","COPY",BODY,{"derivedFrom":makeQuery(id+"F9.opExtrude","SWEPT_BODY",BODY,{"disambiguationData":[OSD([sQuery(id+"F8.wireOp",EDGE,"E7.0"),sQuery(id+"F8.wireOp",EDGE,"E10"),sQuery(id+"F8.wireOp",EDGE,"E11"),sQuery(id+"F8.wireOp",EDGE,"E12.1.0"),sQuery(id+"F8.wireOp",EDGE,"E12.1.1"),sQuery(id+"F8.wireOp",EDGE,"E12.2.0"),sQuery(id+"F8.wireOp",EDGE,"E12.2.1"),sQuery(id+"F8.wireOp",EDGE,"E12.3.0"),sQuery(id+"F8.wireOp",EDGE,"E12.3.1"),sQuery(id+"F8.wireOp",EDGE,"E12.4.0"),sQuery(id+"F8.wireOp",EDGE,"E12.4.1"),sQuery(id+"F8.wireOp",EDGE,"E12.5.0"),sQuery(id+"F8.wireOp",EDGE,"E12.5.1"),sQuery(id+"F8.wireOp",EDGE,"E12.6.0"),sQuery(id+"F8.wireOp",EDGE,"E13"),sQuery(id+"F8.wireOp",EDGE,"E14")])]}),"instanceName":"1"}),"instanceName":"1"}),"instanceName":"2"});
            deleteBodies(context, id + "F64", {"entities" : qUnion([Q0])});
        }
    });
